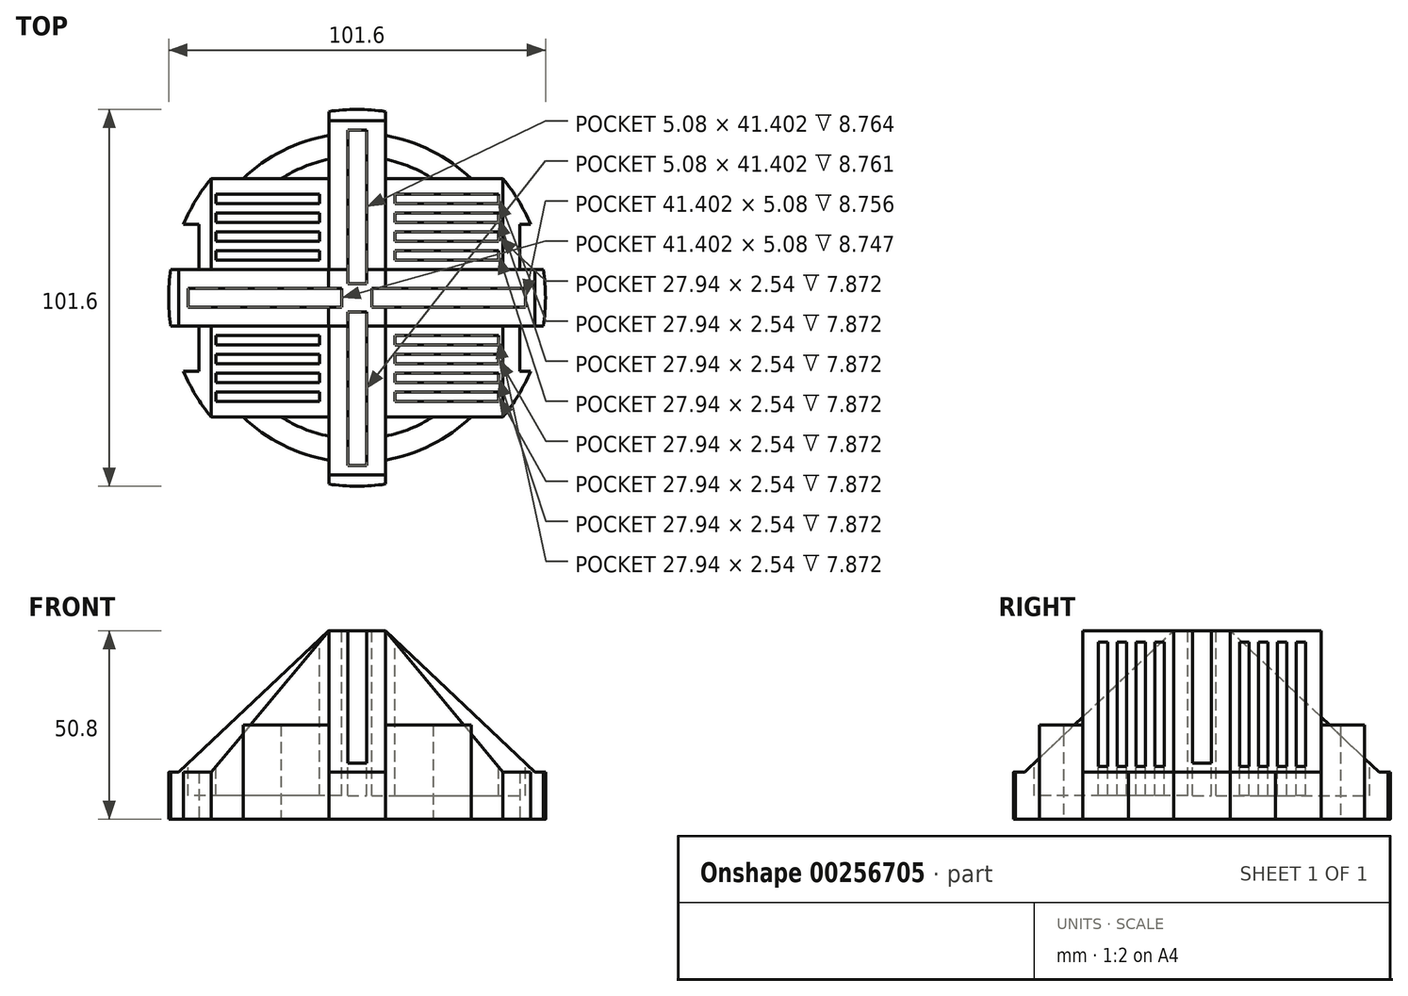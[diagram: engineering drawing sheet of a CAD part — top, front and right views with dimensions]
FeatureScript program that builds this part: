
annotation { "Feature Type Name" : "Feature", "Feature Type Description" : "" }
export const myFeature = defineFeature(function(context is Context, id is Id, definition is map)
    precondition{}
    {
        {
            var Q0;
            Q0=qCreatedBy(makeId("Top.planeOp"),FACE);
            cPlane(context, id + "F0", {"entities" : qUnion([Q0]), "cplaneType" : CPlaneType.OFFSET, "offset" : 50.8 * mm, "width" : 152.4 * mm, "height" : 152.4 * mm});
        }
        {
            var Q0;
            Q0=qCreatedBy(makeId("Top.planeOp"),FACE);
            var sketch = newSketch(context, id + "F1", { "sketchPlane" : qUnion([Q0])});
            skCircle(sketch, "E0", {"center": v(0, 0) * mm, "radius": 50.8 * mm});
            skArc(sketch, "E1", {"start": v(7.62, -43.8) * mm, "mid": v(26.54, -35.66) * mm, "end": v(39.77, -19.86) * mm});
            skArc(sketch, "E2", {"start": v(7.62, -37.33) * mm, "mid": v(38.1, 0) * mm, "end": v(7.62, 37.33) * mm});
            skCircle(sketch, "E3", {"center": v(0, 0) * mm, "radius": 25.4 * mm});
            skLineSegment(sketch, "E4", {"start": v(-7.62, -24.23) * mm, "end": v(-7.62, -50.23) * mm});
            skLineSegment(sketch, "E5", {"start": v(7.62, -24.23) * mm, "end": v(7.62, -50.23) * mm});
            skLineSegment(sketch, "E6", {"start": v(-7.62, 24.23) * mm, "end": v(-7.62, 50.23) * mm});
            skLineSegment(sketch, "E7", {"start": v(7.62, 24.23) * mm, "end": v(7.62, 50.23) * mm});
            skPoint(sketch, "E8.orphan", {"position": v(0, -25.4) * mm});
            skPoint(sketch, "E9.end.orphan", {"position": v(-3.8, -50.66) * mm});
            skArc(sketch, "E10.trimOffspring", {"start": v(-7.62, 37.33) * mm, "mid": v(-38.1, 0) * mm, "end": v(-7.62, -37.33) * mm});
            skArc(sketch, "E11.trimOffspring", {"start": v(-7.62, 43.8) * mm, "mid": v(-26.54, 35.66) * mm, "end": v(-39.77, 19.86) * mm});
            skArc(sketch, "E12", {"start": v(-7.62, -43.8) * mm, "mid": v(0, -44.45) * mm, "end": v(7.62, -43.8) * mm});
            skArc(sketch, "E13", {"start": v(-7.62, -37.33) * mm, "mid": v(0, -38.1) * mm, "end": v(7.62, -37.33) * mm});
            skCircle(sketch, "E14", {"center": v(0, 0) * mm, "radius": 31.75 * mm});
            skArc(sketch, "E15.trimOffspring", {"start": v(7.62, 43.8) * mm, "mid": v(0, 44.45) * mm, "end": v(-7.62, 43.8) * mm});
            skArc(sketch, "E16.trimOffspring", {"start": v(7.62, 37.33) * mm, "mid": v(0, 38.1) * mm, "end": v(-7.62, 37.33) * mm});
            skLineSegment(sketch, "E17", {"start": v(-7.62, -24.23) * mm, "end": v(-7.62, 24.23) * mm});
            skLineSegment(sketch, "E18", {"start": v(7.62, 24.23) * mm, "end": v(7.62, -24.23) * mm});
            skLineSegment(sketch, "E19", {"start": v(0, 7.62) * mm, "end": v(-50.23, 7.62) * mm});
            skLineSegment(sketch, "E20", {"start": v(0, 7.62) * mm, "end": v(50.23, 7.62) * mm});
            skLineSegment(sketch, "E21", {"start": v(0, -7.62) * mm, "end": v(50.23, -7.62) * mm});
            skLineSegment(sketch, "E22", {"start": v(0, -7.62) * mm, "end": v(-50.23, -7.62) * mm});
            skLineSegment(sketch, "E23", {"start": v(-17.78, 7.62) * mm, "end": v(7.62, -17.78) * mm});
            skLineSegment(sketch, "E24", {"start": v(-7.62, 17.78) * mm, "end": v(17.78, -7.62) * mm});
            skLineSegment(sketch, "E25", {"start": v(7.62, 17.78) * mm, "end": v(-17.78, -7.62) * mm});
            skLineSegment(sketch, "E26", {"start": v(17.78, 7.62) * mm, "end": v(-7.62, -17.78) * mm});
            skLineSegment(sketch, "E27", {"start": v(-7.62, -19.86) * mm, "end": v(-20.32, -19.86) * mm});
            skLineSegment(sketch, "E28", {"start": v(-20.32, -19.86) * mm, "end": v(-46.76, -19.86) * mm});
            skLineSegment(sketch, "E29.trimOffspring", {"start": v(-20.32, -32.1) * mm, "end": v(-20.32, -32.23) * mm});
            skPoint(sketch, "E30.start.orphan", {"position": v(-20.32, -7.62) * mm});
            skLineSegment(sketch, "E31", {"start": v(-7.62, -32.1) * mm, "end": v(-39.37, -32.1) * mm});
            skLineSegment(sketch, "E32", {"start": v(-7.62, 19.86) * mm, "end": v(-46.76, 19.86) * mm});
            skLineSegment(sketch, "E33", {"start": v(-7.62, 32.1) * mm, "end": v(-39.37, 32.1) * mm});
            skLineSegment(sketch, "E34", {"start": v(7.62, 32.1) * mm, "end": v(39.37, 32.1) * mm});
            skLineSegment(sketch, "E35", {"start": v(7.62, 19.86) * mm, "end": v(46.76, 19.86) * mm});
            skLineSegment(sketch, "E36", {"start": v(7.62, -19.86) * mm, "end": v(46.76, -19.86) * mm});
            skLineSegment(sketch, "E37", {"start": v(7.62, -32.1) * mm, "end": v(39.37, -32.1) * mm});
            skLineSegment(sketch, "E38", {"start": v(-42.64, 19.86) * mm, "end": v(-42.64, -19.86) * mm});
            skArc(sketch, "E39.trimOffspring", {"start": v(-39.77, -19.86) * mm, "mid": v(-26.54, -35.66) * mm, "end": v(-7.62, -43.8) * mm});
            skLineSegment(sketch, "E40", {"start": v(43.89, -19.86) * mm, "end": v(43.89, 19.86) * mm});
            skArc(sketch, "E41.trimOffspring", {"start": v(39.77, 19.86) * mm, "mid": v(26.54, 35.66) * mm, "end": v(7.62, 43.8) * mm});
            skSolve(sketch);
        }
        {
            var Q0;
            {var subQ5=sQuery(id+"F1.wireOp",EDGE,"E15.trimOffspring");Q0=makeQuery(id+"F1.imprint","IMPRINT",FACE,{"disambiguationData":[TD([[makeQuery(id+"F1.imprint","IMPRINT",EDGE,{"derivedFrom":subQ5}),-1.0]])]});}
            var Q1;
            {var subQ5=sQuery(id+"F1.wireOp",EDGE,"E12");Q1=makeQuery(id+"F1.imprint","IMPRINT",FACE,{"disambiguationData":[TD([[makeQuery(id+"F1.imprint","IMPRINT",EDGE,{"derivedFrom":subQ5}),-1.0]])]});}
            var Q2;
            {var subQ0=sQuery(id+"F1.wireOp",EDGE,"E32");var subQ6=sQuery(id+"F1.wireOp",EDGE,"E0");var subQ7=makeQuery(id+"F1.imprint","INTERSECT",VERTEX,{"derivedFrom":[subQ6,subQ0]});Q2=makeQuery(id+"F1.imprint","IMPRINT",FACE,{"disambiguationData":[TD([[makeQuery(id+"F1.imprint","IMPRINT",EDGE,{"disambiguationData":[TD([[subQ7,1.0]])],"derivedFrom":subQ6}),1.0]])]});}
            var Q3;
            {var subQ0=sQuery(id+"F1.wireOp",EDGE,"E19");var subQ1=sQuery(id+"F1.wireOp",EDGE,"E0");var subQ2=makeQuery(id+"F1.imprint","INTERSECT",VERTEX,{"derivedFrom":[subQ1,subQ0]});Q3=makeQuery(id+"F1.imprint","IMPRINT",FACE,{"disambiguationData":[TD([[makeQuery(id+"F1.imprint","IMPRINT",EDGE,{"disambiguationData":[TD([[subQ2,1.0]])],"derivedFrom":subQ1}),1.0]])]});}
            var Q4;
            {var subQ0=sQuery(id+"F1.wireOp",EDGE,"E19");var subQ1=sQuery(id+"F1.wireOp",EDGE,"E0");var subQ2=makeQuery(id+"F1.imprint","INTERSECT",VERTEX,{"derivedFrom":[subQ1,subQ0]});Q4=makeQuery(id+"F1.imprint","IMPRINT",FACE,{"disambiguationData":[TD([[makeQuery(id+"F1.imprint","IMPRINT",EDGE,{"disambiguationData":[TD([[subQ2,-1.0]])],"derivedFrom":subQ1}),1.0]])]});}
            var Q5;
            {var subQ0=sQuery(id+"F1.wireOp",EDGE,"E22");var subQ1=sQuery(id+"F1.wireOp",EDGE,"E0");var subQ2=makeQuery(id+"F1.imprint","INTERSECT",VERTEX,{"derivedFrom":[subQ1,subQ0]});Q5=makeQuery(id+"F1.imprint","IMPRINT",FACE,{"disambiguationData":[TD([[makeQuery(id+"F1.imprint","IMPRINT",EDGE,{"disambiguationData":[TD([[subQ2,-1.0]])],"derivedFrom":subQ1}),1.0]])]});}
            var Q6;
            {var subQ0=sQuery(id+"F1.wireOp",EDGE,"E28");var subQ4=sQuery(id+"F1.wireOp",EDGE,"E0");var subQ5=makeQuery(id+"F1.imprint","INTERSECT",VERTEX,{"derivedFrom":[subQ4,subQ0]});Q6=makeQuery(id+"F1.imprint","IMPRINT",FACE,{"disambiguationData":[TD([[makeQuery(id+"F1.imprint","IMPRINT",EDGE,{"disambiguationData":[TD([[subQ5,-1.0]])],"derivedFrom":subQ4}),1.0]])]});}
            var Q7;
            {var subQ1=sQuery(id+"F1.wireOp",EDGE,"E0");var subQ6=sQuery(id+"F1.wireOp",EDGE,"E34");var subQ8=makeQuery(id+"F1.imprint","INTERSECT",VERTEX,{"derivedFrom":[subQ1,subQ6]});Q7=makeQuery(id+"F1.imprint","IMPRINT",FACE,{"disambiguationData":[TD([[makeQuery(id+"F1.imprint","IMPRINT",EDGE,{"disambiguationData":[TD([[subQ8,1.0]])],"derivedFrom":subQ1}),1.0]])]});}
            var Q8;
            {var subQ0=sQuery(id+"F1.wireOp",EDGE,"E20");var subQ1=sQuery(id+"F1.wireOp",EDGE,"E0");var subQ2=makeQuery(id+"F1.imprint","INTERSECT",VERTEX,{"derivedFrom":[subQ1,subQ0]});Q8=makeQuery(id+"F1.imprint","IMPRINT",FACE,{"disambiguationData":[TD([[makeQuery(id+"F1.imprint","IMPRINT",EDGE,{"disambiguationData":[TD([[subQ2,-1.0]])],"derivedFrom":subQ1}),1.0]])]});}
            var Q9;
            {var subQ1=sQuery(id+"F1.wireOp",EDGE,"E0");var subQ5=sQuery(id+"F1.wireOp",EDGE,"E20");var subQ6=makeQuery(id+"F1.imprint","INTERSECT",VERTEX,{"derivedFrom":[subQ1,subQ5]});Q9=makeQuery(id+"F1.imprint","IMPRINT",FACE,{"disambiguationData":[TD([[makeQuery(id+"F1.imprint","IMPRINT",EDGE,{"disambiguationData":[TD([[subQ6,1.0]])],"derivedFrom":subQ1}),1.0]])]});}
            var Q10;
            {var subQ0=sQuery(id+"F1.wireOp",EDGE,"E21");var subQ1=sQuery(id+"F1.wireOp",EDGE,"E0");var subQ2=makeQuery(id+"F1.imprint","INTERSECT",VERTEX,{"derivedFrom":[subQ1,subQ0]});Q10=makeQuery(id+"F1.imprint","IMPRINT",FACE,{"disambiguationData":[TD([[makeQuery(id+"F1.imprint","IMPRINT",EDGE,{"disambiguationData":[TD([[subQ2,1.0]])],"derivedFrom":subQ1}),1.0]])]});}
            var Q11;
            {var subQ0=sQuery(id+"F1.wireOp",EDGE,"E36");var subQ1=sQuery(id+"F1.wireOp",EDGE,"E0");var subQ2=makeQuery(id+"F1.imprint","INTERSECT",VERTEX,{"derivedFrom":[subQ1,subQ0]});Q11=makeQuery(id+"F1.imprint","IMPRINT",FACE,{"disambiguationData":[TD([[makeQuery(id+"F1.imprint","IMPRINT",EDGE,{"disambiguationData":[TD([[subQ2,1.0]])],"derivedFrom":subQ1}),1.0]])]});}
            var Q12;
            {var subQ0=sQuery(id+"F1.wireOp",EDGE,"E4");var subQ1=sQuery(id+"F1.wireOp",EDGE,"E0");var subQ2=makeQuery(id+"F1.imprint","INTERSECT",VERTEX,{"derivedFrom":[subQ1,subQ0]});Q12=makeQuery(id+"F1.imprint","IMPRINT",FACE,{"disambiguationData":[TD([[makeQuery(id+"F1.imprint","IMPRINT",EDGE,{"disambiguationData":[TD([[subQ2,1.0]])],"derivedFrom":subQ1}),1.0]])]});}
            var Q13;
            {var subQ0=sQuery(id+"F1.wireOp",EDGE,"E6");var subQ1=sQuery(id+"F1.wireOp",EDGE,"E0");var subQ2=makeQuery(id+"F1.imprint","INTERSECT",VERTEX,{"derivedFrom":[subQ1,subQ0]});Q13=makeQuery(id+"F1.imprint","IMPRINT",FACE,{"disambiguationData":[TD([[makeQuery(id+"F1.imprint","IMPRINT",EDGE,{"disambiguationData":[TD([[subQ2,-1.0]])],"derivedFrom":subQ1}),1.0]])]});}
            var Q14;
            {var subQ0=sQuery(id+"F1.wireOp",EDGE,"E7");var subQ1=sQuery(id+"F1.wireOp",EDGE,"E0");var subQ2=makeQuery(id+"F1.imprint","INTERSECT",VERTEX,{"derivedFrom":[subQ1,subQ0]});Q14=makeQuery(id+"F1.imprint","IMPRINT",FACE,{"disambiguationData":[TD([[makeQuery(id+"F1.imprint","IMPRINT",EDGE,{"disambiguationData":[TD([[subQ2,1.0]])],"derivedFrom":subQ1}),1.0]])]});}
            var Q15;
            {var subQ0=sQuery(id+"F1.wireOp",EDGE,"E5");var subQ1=sQuery(id+"F1.wireOp",EDGE,"E0");var subQ2=makeQuery(id+"F1.imprint","INTERSECT",VERTEX,{"derivedFrom":[subQ1,subQ0]});Q15=makeQuery(id+"F1.imprint","IMPRINT",FACE,{"disambiguationData":[TD([[makeQuery(id+"F1.imprint","IMPRINT",EDGE,{"disambiguationData":[TD([[subQ2,-1.0]])],"derivedFrom":subQ1}),1.0]])]});}
            extrude(context, id + "F2", {"entities" : qUnion([Q0, Q1, Q2, Q3, Q4, Q5, Q6, Q7, Q8, Q9, Q10, Q11, Q12, Q13, Q14, Q15]), "depth" : 12.7 * mm});
        }
        {
            var Q0;
            {var subQ0=sQuery(id+"F1.wireOp",EDGE,"E10.trimOffspring");Q0=makeQuery(id+"F1.imprint","IMPRINT",FACE,{"disambiguationData":[TD([[makeQuery(id+"F1.imprint","IMPRINT",EDGE,{"derivedFrom":subQ0}),-1.0]])]});}
            var Q1;
            {var subQ0=sQuery(id+"F1.wireOp",EDGE,"E1");Q1=makeQuery(id+"F1.imprint","IMPRINT",FACE,{"disambiguationData":[TD([[makeQuery(id+"F1.imprint","IMPRINT",EDGE,{"derivedFrom":subQ0}),1.0]])]});}
            var Q2;
            {var subQ2=sQuery(id+"F1.wireOp",EDGE,"E15.trimOffspring");Q2=makeQuery(id+"F1.imprint","IMPRINT",FACE,{"disambiguationData":[TD([[makeQuery(id+"F1.imprint","IMPRINT",EDGE,{"derivedFrom":subQ2}),1.0]])]});}
            var Q3;
            {var subQ2=sQuery(id+"F1.wireOp",EDGE,"E12");Q3=makeQuery(id+"F1.imprint","IMPRINT",FACE,{"disambiguationData":[TD([[makeQuery(id+"F1.imprint","IMPRINT",EDGE,{"derivedFrom":subQ2}),1.0]])]});}
            var Q4;
            {var subQ0=sQuery(id+"F1.wireOp",EDGE,"E10.trimOffspring");var subQ5=sQuery(id+"F1.wireOp",EDGE,"KU0cdiGB-8eOj-Trs3-v5YD-3LzdnCRRimhK");var subQ6=makeQuery(id+"F1.imprint","INTERSECT",VERTEX,{"derivedFrom":[subQ0,subQ5]});Q4=makeQuery(id+"F1.imprint","IMPRINT",FACE,{"disambiguationData":[TD([[makeQuery(id+"F1.imprint","IMPRINT",EDGE,{"disambiguationData":[TD([[subQ6,-1.0]])],"derivedFrom":subQ5}),-1.0]])]});}
            var Q5;
            {var subQ0=sQuery(id+"F1.wireOp",EDGE,"KU0cdiGB-8eOj-Trs3-v5YD-3LzdnCRRimhK");var subQ1=sQuery(id+"F1.wireOp",EDGE,"E10.trimOffspring");var subQ2=makeQuery(id+"F1.imprint","INTERSECT",VERTEX,{"derivedFrom":[subQ1,subQ0]});Q5=makeQuery(id+"F1.imprint","IMPRINT",FACE,{"disambiguationData":[TD([[makeQuery(id+"F1.imprint","IMPRINT",EDGE,{"disambiguationData":[TD([[subQ2,-1.0]])],"derivedFrom":subQ1}),-1.0]])]});}
            var Q6;
            {var subQ0=sQuery(id+"F1.wireOp",EDGE,"n5LII22h-w08l-qE72-yfr9-18N67uZxNTdQ");var subQ1=sQuery(id+"F1.wireOp",EDGE,"E10.trimOffspring");var subQ2=makeQuery(id+"F1.imprint","INTERSECT",VERTEX,{"derivedFrom":[subQ1,subQ0]});Q6=makeQuery(id+"F1.imprint","IMPRINT",FACE,{"disambiguationData":[TD([[makeQuery(id+"F1.imprint","IMPRINT",EDGE,{"disambiguationData":[TD([[subQ2,-1.0]])],"derivedFrom":subQ1}),-1.0]])]});}
            var Q7;
            {var subQ0=sQuery(id+"F1.wireOp",EDGE,"E19");var subQ1=sQuery(id+"F1.wireOp",EDGE,"E10.trimOffspring");var subQ2=makeQuery(id+"F1.imprint","INTERSECT",VERTEX,{"derivedFrom":[subQ1,subQ0]});Q7=makeQuery(id+"F1.imprint","IMPRINT",FACE,{"disambiguationData":[TD([[makeQuery(id+"F1.imprint","IMPRINT",EDGE,{"disambiguationData":[TD([[subQ2,-1.0]])],"derivedFrom":subQ1}),-1.0]])]});}
            var Q8;
            {var subQ0=sQuery(id+"F1.wireOp",EDGE,"E22");var subQ1=sQuery(id+"F1.wireOp",EDGE,"E10.trimOffspring");var subQ2=makeQuery(id+"F1.imprint","INTERSECT",VERTEX,{"derivedFrom":[subQ1,subQ0]});Q8=makeQuery(id+"F1.imprint","IMPRINT",FACE,{"disambiguationData":[TD([[makeQuery(id+"F1.imprint","IMPRINT",EDGE,{"disambiguationData":[TD([[subQ2,-1.0]])],"derivedFrom":subQ1}),-1.0]])]});}
            var Q9;
            {var subQ0=sQuery(id+"F1.wireOp",EDGE,"E28");var subQ1=sQuery(id+"F1.wireOp",EDGE,"E10.trimOffspring");var subQ2=makeQuery(id+"F1.imprint","INTERSECT",VERTEX,{"derivedFrom":[subQ1,subQ0]});Q9=makeQuery(id+"F1.imprint","IMPRINT",FACE,{"disambiguationData":[TD([[makeQuery(id+"F1.imprint","IMPRINT",EDGE,{"disambiguationData":[TD([[subQ2,-1.0]])],"derivedFrom":subQ1}),-1.0]])]});}
            var Q10;
            {var subQ1=sQuery(id+"F1.wireOp",EDGE,"E10.trimOffspring");var subQ5=sQuery(id+"F1.wireOp",EDGE,"E25");var subQ6=makeQuery(id+"F1.imprint","INTERSECT",VERTEX,{"derivedFrom":[subQ1,subQ5]});Q10=makeQuery(id+"F1.imprint","IMPRINT",FACE,{"disambiguationData":[TD([[makeQuery(id+"F1.imprint","IMPRINT",EDGE,{"disambiguationData":[TD([[subQ6,-1.0]])],"derivedFrom":subQ1}),-1.0]])]});}
            var Q11;
            {var subQ0=sQuery(id+"F1.wireOp",EDGE,"E31");var subQ1=sQuery(id+"F1.wireOp",EDGE,"E11.trimOffspring");var subQ2=makeQuery(id+"F1.imprint","INTERSECT",VERTEX,{"derivedFrom":[subQ1,subQ0]});Q11=makeQuery(id+"F1.imprint","IMPRINT",FACE,{"disambiguationData":[TD([[makeQuery(id+"F1.imprint","IMPRINT",EDGE,{"disambiguationData":[TD([[subQ2,-1.0]])],"derivedFrom":subQ1}),1.0]])]});}
            var Q12;
            {var subQ0=sQuery(id+"F1.wireOp",EDGE,"E26");var subQ1=sQuery(id+"F1.wireOp",EDGE,"E10.trimOffspring");var subQ2=makeQuery(id+"F1.imprint","INTERSECT",VERTEX,{"derivedFrom":[subQ1,subQ0]});Q12=makeQuery(id+"F1.imprint","IMPRINT",FACE,{"disambiguationData":[TD([[makeQuery(id+"F1.imprint","IMPRINT",EDGE,{"disambiguationData":[TD([[subQ2,-1.0]])],"derivedFrom":subQ1}),-1.0]])]});}
            var Q13;
            {var subQ0=sQuery(id+"F1.wireOp",EDGE,"E32");var subQ1=sQuery(id+"F1.wireOp",EDGE,"E10.trimOffspring");var subQ2=makeQuery(id+"F1.imprint","INTERSECT",VERTEX,{"derivedFrom":[subQ1,subQ0]});Q13=makeQuery(id+"F1.imprint","IMPRINT",FACE,{"disambiguationData":[TD([[makeQuery(id+"F1.imprint","IMPRINT",EDGE,{"disambiguationData":[TD([[subQ2,-1.0]])],"derivedFrom":subQ1}),-1.0]])]});}
            var Q14;
            {var subQ0=sQuery(id+"F1.wireOp",EDGE,"E33");var subQ1=sQuery(id+"F1.wireOp",EDGE,"E10.trimOffspring");var subQ2=makeQuery(id+"F1.imprint","INTERSECT",VERTEX,{"derivedFrom":[subQ1,subQ0]});Q14=makeQuery(id+"F1.imprint","IMPRINT",FACE,{"disambiguationData":[TD([[makeQuery(id+"F1.imprint","IMPRINT",EDGE,{"disambiguationData":[TD([[subQ2,-1.0]])],"derivedFrom":subQ1}),-1.0]])]});}
            var Q15;
            {var subQ0=sQuery(id+"F1.wireOp",EDGE,"E10.trimOffspring");var subQ5=sQuery(id+"F1.wireOp",EDGE,"E33");var subQ7=makeQuery(id+"F1.imprint","INTERSECT",VERTEX,{"derivedFrom":[subQ0,subQ5]});Q15=makeQuery(id+"F1.imprint","IMPRINT",FACE,{"disambiguationData":[TD([[makeQuery(id+"F1.imprint","IMPRINT",EDGE,{"disambiguationData":[TD([[subQ7,-1.0]])],"derivedFrom":subQ5}),-1.0]])]});}
            var Q16;
            {var subQ0=sQuery(id+"F1.wireOp",EDGE,"E35");var subQ1=sQuery(id+"F1.wireOp",EDGE,"E2");var subQ2=makeQuery(id+"F1.imprint","INTERSECT",VERTEX,{"derivedFrom":[subQ1,subQ0]});Q16=makeQuery(id+"F1.imprint","IMPRINT",FACE,{"disambiguationData":[TD([[makeQuery(id+"F1.imprint","IMPRINT",EDGE,{"disambiguationData":[TD([[subQ2,-1.0]])],"derivedFrom":subQ1}),-1.0]])]});}
            var Q17;
            {var subQ0=sQuery(id+"F1.wireOp",EDGE,"E20");var subQ6=sQuery(id+"F1.wireOp",EDGE,"E2");var subQ8=makeQuery(id+"F1.imprint","INTERSECT",VERTEX,{"derivedFrom":[subQ6,subQ0]});Q17=makeQuery(id+"F1.imprint","IMPRINT",FACE,{"disambiguationData":[TD([[makeQuery(id+"F1.imprint","IMPRINT",EDGE,{"disambiguationData":[TD([[subQ8,-1.0]])],"derivedFrom":subQ6}),-1.0]])]});}
            var Q18;
            {var subQ0=sQuery(id+"F1.wireOp",EDGE,"18cd6810-feed-407b-96fd-876ede30ebc9.trimOffspring");Q18=makeQuery(id+"F1.imprint","IMPRINT",FACE,{"disambiguationData":[TD([[makeQuery(id+"F1.imprint","IMPRINT",EDGE,{"derivedFrom":subQ0}),1.0]])]});}
            var Q19;
            {var subQ0=sQuery(id+"F1.wireOp",EDGE,"E36");var subQ2=sQuery(id+"F1.wireOp",EDGE,"E2");var subQ3=makeQuery(id+"F1.imprint","INTERSECT",VERTEX,{"derivedFrom":[subQ2,subQ0]});Q19=makeQuery(id+"F1.imprint","IMPRINT",FACE,{"disambiguationData":[TD([[makeQuery(id+"F1.imprint","IMPRINT",EDGE,{"disambiguationData":[TD([[subQ3,-1.0]])],"derivedFrom":subQ2}),-1.0]])]});}
            var Q20;
            {var subQ0=sQuery(id+"F1.wireOp",EDGE,"E21");var subQ1=sQuery(id+"F1.wireOp",EDGE,"E2");var subQ2=makeQuery(id+"F1.imprint","INTERSECT",VERTEX,{"derivedFrom":[subQ1,subQ0]});Q20=makeQuery(id+"F1.imprint","IMPRINT",FACE,{"disambiguationData":[TD([[makeQuery(id+"F1.imprint","IMPRINT",EDGE,{"disambiguationData":[TD([[subQ2,-1.0]])],"derivedFrom":subQ1}),-1.0]])]});}
            var Q21;
            {var subQ1=sQuery(id+"F1.wireOp",EDGE,"E2");var subQ3=sQuery(id+"F1.wireOp",EDGE,"E34");var subQ4=makeQuery(id+"F1.imprint","INTERSECT",VERTEX,{"derivedFrom":[subQ1,subQ3]});Q21=makeQuery(id+"F1.imprint","IMPRINT",FACE,{"disambiguationData":[TD([[makeQuery(id+"F1.imprint","IMPRINT",EDGE,{"disambiguationData":[TD([[subQ4,-1.0]])],"derivedFrom":subQ3}),1.0]])]});}
            extrude(context, id + "F3", {"entities" : qUnion([Q0, Q1, Q2, Q3, Q4, Q5, Q6, Q7, Q8, Q9, Q10, Q11, Q12, Q13, Q14, Q15, Q16, Q17, Q18, Q19, Q20, Q21]), "operationType" : NewBodyOperationType.ADD, "depth" : 25.4 * mm});
        }
        {
            var Q0;
            {var subQ0=sQuery(id+"F1.wireOp",EDGE,"E13");Q0=makeQuery(id+"F1.imprint","IMPRINT",FACE,{"disambiguationData":[TD([[makeQuery(id+"F1.imprint","IMPRINT",EDGE,{"derivedFrom":subQ0}),1.0]])]});}
            var Q1;
            {var subQ0=sQuery(id+"F1.wireOp",EDGE,"E10.trimOffspring");Q1=makeQuery(id+"F1.imprint","IMPRINT",FACE,{"disambiguationData":[TD([[makeQuery(id+"F1.imprint","IMPRINT",EDGE,{"derivedFrom":subQ0}),1.0]])]});}
            var Q2;
            {var subQ0=sQuery(id+"F1.wireOp",EDGE,"E2");Q2=makeQuery(id+"F1.imprint","IMPRINT",FACE,{"disambiguationData":[TD([[makeQuery(id+"F1.imprint","IMPRINT",EDGE,{"derivedFrom":subQ0}),1.0]])]});}
            var Q3;
            {var subQ0=sQuery(id+"F1.wireOp",EDGE,"E16.trimOffspring");Q3=makeQuery(id+"F1.imprint","IMPRINT",FACE,{"disambiguationData":[TD([[makeQuery(id+"F1.imprint","IMPRINT",EDGE,{"derivedFrom":subQ0}),1.0]])]});}
            var Q4;
            {var subQ0=sQuery(id+"F1.wireOp",EDGE,"n5LII22h-w08l-qE72-yfr9-18N67uZxNTdQ");var subQ1=sQuery(id+"F1.wireOp",EDGE,"E10.trimOffspring");var subQ2=makeQuery(id+"F1.imprint","INTERSECT",VERTEX,{"derivedFrom":[subQ1,subQ0]});Q4=makeQuery(id+"F1.imprint","IMPRINT",FACE,{"disambiguationData":[TD([[makeQuery(id+"F1.imprint","IMPRINT",EDGE,{"disambiguationData":[TD([[subQ2,-1.0]])],"derivedFrom":subQ1}),1.0]])]});}
            var Q5;
            {var subQ0=sQuery(id+"F1.wireOp",EDGE,"KU0cdiGB-8eOj-Trs3-v5YD-3LzdnCRRimhK");var subQ1=sQuery(id+"F1.wireOp",EDGE,"E10.trimOffspring");var subQ2=makeQuery(id+"F1.imprint","INTERSECT",VERTEX,{"derivedFrom":[subQ1,subQ0]});Q5=makeQuery(id+"F1.imprint","IMPRINT",FACE,{"disambiguationData":[TD([[makeQuery(id+"F1.imprint","IMPRINT",EDGE,{"disambiguationData":[TD([[subQ2,-1.0]])],"derivedFrom":subQ1}),1.0]])]});}
            var Q6;
            {var subQ1=sQuery(id+"F1.wireOp",EDGE,"E6");var subQ3=sQuery(id+"F1.wireOp",EDGE,"E14");var subQ4=makeQuery(id+"F1.imprint","INTERSECT",VERTEX,{"derivedFrom":[subQ1,subQ3]});Q6=makeQuery(id+"F1.imprint","IMPRINT",FACE,{"disambiguationData":[TD([[makeQuery(id+"F1.imprint","IMPRINT",EDGE,{"disambiguationData":[TD([[subQ4,-1.0]])],"derivedFrom":subQ3}),-1.0]])]});}
            var Q7;
            {var subQ0=sQuery(id+"F1.wireOp",EDGE,"E7");var subQ5=sQuery(id+"F1.wireOp",EDGE,"E14");var subQ6=makeQuery(id+"F1.imprint","INTERSECT",VERTEX,{"derivedFrom":[subQ0,subQ5]});Q7=makeQuery(id+"F1.imprint","IMPRINT",FACE,{"disambiguationData":[TD([[makeQuery(id+"F1.imprint","IMPRINT",EDGE,{"disambiguationData":[TD([[subQ6,1.0]])],"derivedFrom":subQ5}),-1.0]])]});}
            var Q8;
            {var subQ0=sQuery(id+"F1.wireOp",EDGE,"E19");var subQ1=sQuery(id+"F1.wireOp",EDGE,"E10.trimOffspring");var subQ2=makeQuery(id+"F1.imprint","INTERSECT",VERTEX,{"derivedFrom":[subQ1,subQ0]});Q8=makeQuery(id+"F1.imprint","IMPRINT",FACE,{"disambiguationData":[TD([[makeQuery(id+"F1.imprint","IMPRINT",EDGE,{"disambiguationData":[TD([[subQ2,-1.0]])],"derivedFrom":subQ1}),1.0]])]});}
            var Q9;
            {var subQ0=sQuery(id+"F1.wireOp",EDGE,"E22");var subQ1=sQuery(id+"F1.wireOp",EDGE,"E10.trimOffspring");var subQ2=makeQuery(id+"F1.imprint","INTERSECT",VERTEX,{"derivedFrom":[subQ1,subQ0]});Q9=makeQuery(id+"F1.imprint","IMPRINT",FACE,{"disambiguationData":[TD([[makeQuery(id+"F1.imprint","IMPRINT",EDGE,{"disambiguationData":[TD([[subQ2,-1.0]])],"derivedFrom":subQ1}),1.0]])]});}
            var Q10;
            {var subQ0=sQuery(id+"F1.wireOp",EDGE,"E25");var subQ1=sQuery(id+"F1.wireOp",EDGE,"E10.trimOffspring");var subQ2=makeQuery(id+"F1.imprint","INTERSECT",VERTEX,{"derivedFrom":[subQ1,subQ0]});Q10=makeQuery(id+"F1.imprint","IMPRINT",FACE,{"disambiguationData":[TD([[makeQuery(id+"F1.imprint","IMPRINT",EDGE,{"disambiguationData":[TD([[subQ2,-1.0]])],"derivedFrom":subQ1}),1.0]])]});}
            var Q11;
            {var subQ3=sQuery(id+"F1.wireOp",EDGE,"E14");var subQ7=sQuery(id+"F1.wireOp",EDGE,"E4");var subQ8=makeQuery(id+"F1.imprint","INTERSECT",VERTEX,{"derivedFrom":[subQ7,subQ3]});Q11=makeQuery(id+"F1.imprint","IMPRINT",FACE,{"disambiguationData":[TD([[makeQuery(id+"F1.imprint","IMPRINT",EDGE,{"disambiguationData":[TD([[subQ8,-1.0]])],"derivedFrom":subQ7}),-1.0]])]});}
            var Q12;
            {var subQ1=sQuery(id+"F1.wireOp",EDGE,"E2");var subQ5=sQuery(id+"F1.wireOp",EDGE,"dChad7VG-r3lr-Y0ra-zuCQ-UW0r8UzcO7aT");var subQ6=makeQuery(id+"F1.imprint","INTERSECT",VERTEX,{"derivedFrom":[subQ1,subQ5]});Q12=makeQuery(id+"F1.imprint","IMPRINT",FACE,{"disambiguationData":[TD([[makeQuery(id+"F1.imprint","IMPRINT",EDGE,{"disambiguationData":[TD([[subQ6,-1.0]])],"derivedFrom":subQ1}),1.0]])]});}
            var Q13;
            {var subQ0=sQuery(id+"F1.wireOp",EDGE,"E23");var subQ1=sQuery(id+"F1.wireOp",EDGE,"E2");var subQ2=makeQuery(id+"F1.imprint","INTERSECT",VERTEX,{"derivedFrom":[subQ1,subQ0]});Q13=makeQuery(id+"F1.imprint","IMPRINT",FACE,{"disambiguationData":[TD([[makeQuery(id+"F1.imprint","IMPRINT",EDGE,{"disambiguationData":[TD([[subQ2,-1.0]])],"derivedFrom":subQ1}),1.0]])]});}
            var Q14;
            {var subQ0=sQuery(id+"F1.wireOp",EDGE,"E24");var subQ1=sQuery(id+"F1.wireOp",EDGE,"E2");var subQ2=makeQuery(id+"F1.imprint","INTERSECT",VERTEX,{"derivedFrom":[subQ1,subQ0]});Q14=makeQuery(id+"F1.imprint","IMPRINT",FACE,{"disambiguationData":[TD([[makeQuery(id+"F1.imprint","IMPRINT",EDGE,{"disambiguationData":[TD([[subQ2,-1.0]])],"derivedFrom":subQ1}),1.0]])]});}
            var Q15;
            {var subQ0=sQuery(id+"F1.wireOp",EDGE,"E21");var subQ1=sQuery(id+"F1.wireOp",EDGE,"E2");var subQ2=makeQuery(id+"F1.imprint","INTERSECT",VERTEX,{"derivedFrom":[subQ1,subQ0]});Q15=makeQuery(id+"F1.imprint","IMPRINT",FACE,{"disambiguationData":[TD([[makeQuery(id+"F1.imprint","IMPRINT",EDGE,{"disambiguationData":[TD([[subQ2,-1.0]])],"derivedFrom":subQ1}),1.0]])]});}
            var Q16;
            {var subQ0=sQuery(id+"F1.wireOp",EDGE,"E20");var subQ1=sQuery(id+"F1.wireOp",EDGE,"E2");var subQ2=makeQuery(id+"F1.imprint","INTERSECT",VERTEX,{"derivedFrom":[subQ1,subQ0]});Q16=makeQuery(id+"F1.imprint","IMPRINT",FACE,{"disambiguationData":[TD([[makeQuery(id+"F1.imprint","IMPRINT",EDGE,{"disambiguationData":[TD([[subQ2,-1.0]])],"derivedFrom":subQ1}),1.0]])]});}
            var Q17;
            {var subQ0=sQuery(id+"F1.wireOp",EDGE,"SVIod6WE-LFFt-Ms97-owyS-8ShU65W6W8it");var subQ1=sQuery(id+"F1.wireOp",EDGE,"E2");var subQ2=makeQuery(id+"F1.imprint","INTERSECT",VERTEX,{"derivedFrom":[subQ1,subQ0]});Q17=makeQuery(id+"F1.imprint","IMPRINT",FACE,{"disambiguationData":[TD([[makeQuery(id+"F1.imprint","IMPRINT",EDGE,{"disambiguationData":[TD([[subQ2,-1.0]])],"derivedFrom":subQ1}),1.0]])]});}
            var Q18;
            {var subQ0=sQuery(id+"F1.wireOp",EDGE,"E25");var subQ1=sQuery(id+"F1.wireOp",EDGE,"E14");var subQ2=makeQuery(id+"F1.imprint","INTERSECT",VERTEX,{"derivedFrom":[subQ1,subQ0]});Q18=makeQuery(id+"F1.imprint","IMPRINT",FACE,{"disambiguationData":[TD([[makeQuery(id+"F1.imprint","IMPRINT",EDGE,{"disambiguationData":[TD([[subQ2,-1.0]])],"derivedFrom":subQ1}),-1.0]])]});}
            var Q19;
            {var subQ0=sQuery(id+"F1.wireOp",EDGE,"E30");var subQ1=sQuery(id+"F1.wireOp",EDGE,"E14");var subQ2=makeQuery(id+"F1.imprint","INTERSECT",VERTEX,{"derivedFrom":[subQ1,subQ0]});Q19=makeQuery(id+"F1.imprint","IMPRINT",FACE,{"disambiguationData":[TD([[makeQuery(id+"F1.imprint","IMPRINT",EDGE,{"disambiguationData":[TD([[subQ2,-1.0]])],"derivedFrom":subQ1}),-1.0]])]});}
            var Q20;
            {var subQ5=sQuery(id+"F1.wireOp",EDGE,"E29.trimOffspring");Q20=makeQuery(id+"F1.imprint","IMPRINT",FACE,{"disambiguationData":[TD([[makeQuery(id+"F1.imprint","IMPRINT",EDGE,{"derivedFrom":subQ5}),1.0]])]});}
            var Q21;
            {var subQ1=sQuery(id+"F1.wireOp",EDGE,"E2");var subQ7=sQuery(id+"F1.wireOp",EDGE,"E37");var subQ9=makeQuery(id+"F1.imprint","INTERSECT",VERTEX,{"derivedFrom":[subQ1,subQ7]});Q21=makeQuery(id+"F1.imprint","IMPRINT",FACE,{"disambiguationData":[TD([[makeQuery(id+"F1.imprint","IMPRINT",EDGE,{"disambiguationData":[TD([[subQ9,-1.0]])],"derivedFrom":subQ1}),1.0]])]});}
            extrude(context, id + "F4", {"entities" : qUnion([Q0, Q1, Q2, Q3, Q4, Q5, Q6, Q7, Q8, Q9, Q10, Q11, Q12, Q13, Q14, Q15, Q16, Q17, Q18, Q19, Q20, Q21]), "operationType" : NewBodyOperationType.ADD, "depth" : 38.1 * mm});
        }
        {
            var Q0;
            {var subQ0=sQuery(id+"F1.wireOp",EDGE,"E6");var subQ1=sQuery(id+"F1.wireOp",EDGE,"E3");var subQ2=makeQuery(id+"F1.imprint","INTERSECT",VERTEX,{"derivedFrom":[subQ1,subQ0]});Q0=makeQuery(id+"F1.imprint","IMPRINT",FACE,{"disambiguationData":[TD([[makeQuery(id+"F1.imprint","IMPRINT",EDGE,{"disambiguationData":[TD([[subQ2,1.0]])],"derivedFrom":subQ1}),-1.0]])]});}
            var Q1;
            {var subQ0=sQuery(id+"F1.wireOp",EDGE,"E4");var subQ1=sQuery(id+"F1.wireOp",EDGE,"E3");var subQ2=makeQuery(id+"F1.imprint","INTERSECT",VERTEX,{"derivedFrom":[subQ1,subQ0]});Q1=makeQuery(id+"F1.imprint","IMPRINT",FACE,{"disambiguationData":[TD([[makeQuery(id+"F1.imprint","IMPRINT",EDGE,{"disambiguationData":[TD([[subQ2,-1.0]])],"derivedFrom":subQ1}),-1.0]])]});}
            var Q2;
            {var subQ0=sQuery(id+"F1.wireOp",EDGE,"E5");var subQ1=sQuery(id+"F1.wireOp",EDGE,"E3");var subQ2=makeQuery(id+"F1.imprint","INTERSECT",VERTEX,{"derivedFrom":[subQ1,subQ0]});Q2=makeQuery(id+"F1.imprint","IMPRINT",FACE,{"disambiguationData":[TD([[makeQuery(id+"F1.imprint","IMPRINT",EDGE,{"disambiguationData":[TD([[subQ2,-1.0]])],"derivedFrom":subQ1}),-1.0]])]});}
            var Q3;
            {var subQ0=sQuery(id+"F1.wireOp",EDGE,"E7");var subQ5=sQuery(id+"F1.wireOp",EDGE,"E14");var subQ6=makeQuery(id+"F1.imprint","INTERSECT",VERTEX,{"derivedFrom":[subQ0,subQ5]});Q3=makeQuery(id+"F1.imprint","IMPRINT",FACE,{"disambiguationData":[TD([[makeQuery(id+"F1.imprint","IMPRINT",EDGE,{"disambiguationData":[TD([[subQ6,1.0]])],"derivedFrom":subQ5}),1.0]])]});}
            var Q4;
            {var subQ0=sQuery(id+"F1.wireOp",EDGE,"E19");var subQ1=sQuery(id+"F1.wireOp",EDGE,"E3");var subQ2=makeQuery(id+"F1.imprint","INTERSECT",VERTEX,{"derivedFrom":[subQ1,subQ0]});Q4=makeQuery(id+"F1.imprint","IMPRINT",FACE,{"disambiguationData":[TD([[makeQuery(id+"F1.imprint","IMPRINT",EDGE,{"disambiguationData":[TD([[subQ2,-1.0]])],"derivedFrom":subQ1}),-1.0]])]});}
            var Q5;
            {var subQ0=sQuery(id+"F1.wireOp",EDGE,"E6");var subQ5=sQuery(id+"F1.wireOp",EDGE,"E14");var subQ6=makeQuery(id+"F1.imprint","INTERSECT",VERTEX,{"derivedFrom":[subQ0,subQ5]});Q5=makeQuery(id+"F1.imprint","IMPRINT",FACE,{"disambiguationData":[TD([[makeQuery(id+"F1.imprint","IMPRINT",EDGE,{"disambiguationData":[TD([[subQ6,-1.0]])],"derivedFrom":subQ5}),1.0]])]});}
            var Q6;
            {var subQ0=sQuery(id+"F1.wireOp",EDGE,"E20");var subQ1=sQuery(id+"F1.wireOp",EDGE,"E3");var subQ2=makeQuery(id+"F1.imprint","INTERSECT",VERTEX,{"derivedFrom":[subQ1,subQ0]});Q6=makeQuery(id+"F1.imprint","IMPRINT",FACE,{"disambiguationData":[TD([[makeQuery(id+"F1.imprint","IMPRINT",EDGE,{"disambiguationData":[TD([[subQ2,1.0]])],"derivedFrom":subQ1}),-1.0]])]});}
            var Q7;
            {var subQ1=sQuery(id+"F1.wireOp",EDGE,"E4");var subQ3=sQuery(id+"F1.wireOp",EDGE,"E14");var subQ4=makeQuery(id+"F1.imprint","INTERSECT",VERTEX,{"derivedFrom":[subQ1,subQ3]});Q7=makeQuery(id+"F1.imprint","IMPRINT",FACE,{"disambiguationData":[TD([[makeQuery(id+"F1.imprint","IMPRINT",EDGE,{"disambiguationData":[TD([[subQ4,1.0]])],"derivedFrom":subQ3}),1.0]])]});}
            var Q8;
            {var subQ3=sQuery(id+"F1.wireOp",EDGE,"6cIBHAnO-3Gdr-gs2R-q8mb-qejxkHO2rhEE");var subQ5=sQuery(id+"F1.wireOp",EDGE,"E14");var subQ6=makeQuery(id+"F1.imprint","INTERSECT",VERTEX,{"derivedFrom":[subQ5,subQ3]});Q8=makeQuery(id+"F1.imprint","IMPRINT",FACE,{"disambiguationData":[TD([[makeQuery(id+"F1.imprint","IMPRINT",EDGE,{"disambiguationData":[TD([[subQ6,-1.0]])],"derivedFrom":subQ5}),1.0]])]});}
            var Q9;
            {var subQ0=sQuery(id+"F1.wireOp",EDGE,"E22");var subQ1=sQuery(id+"F1.wireOp",EDGE,"E14");var subQ2=makeQuery(id+"F1.imprint","INTERSECT",VERTEX,{"derivedFrom":[subQ1,subQ0]});Q9=makeQuery(id+"F1.imprint","IMPRINT",FACE,{"disambiguationData":[TD([[makeQuery(id+"F1.imprint","IMPRINT",EDGE,{"disambiguationData":[TD([[subQ2,-1.0]])],"derivedFrom":subQ1}),1.0]])]});}
            var Q10;
            {var subQ3=sQuery(id+"F1.wireOp",EDGE,"1679b663-5bbc-411f-b373-dbe6ce103e45.trimOffspring");var subQ5=sQuery(id+"F1.wireOp",EDGE,"E14");var subQ7=makeQuery(id+"F1.imprint","INTERSECT",VERTEX,{"disambiguationData":[OD(1.0)],"derivedFrom":[subQ5,subQ3]});Q10=makeQuery(id+"F1.imprint","IMPRINT",FACE,{"disambiguationData":[TD([[makeQuery(id+"F1.imprint","IMPRINT",EDGE,{"disambiguationData":[TD([[subQ7,-1.0]])],"derivedFrom":subQ5}),1.0]])]});}
            var Q11;
            {var subQ3=sQuery(id+"F1.wireOp",EDGE,"8l5Dcz2D-qY2G-ceuh-glFK-kLwJx8DI5XpU");var subQ5=sQuery(id+"F1.wireOp",EDGE,"E14");var subQ7=makeQuery(id+"F1.imprint","INTERSECT",VERTEX,{"derivedFrom":[subQ5,subQ3]});Q11=makeQuery(id+"F1.imprint","IMPRINT",FACE,{"disambiguationData":[TD([[makeQuery(id+"F1.imprint","IMPRINT",EDGE,{"disambiguationData":[TD([[subQ7,-1.0]])],"derivedFrom":subQ5}),1.0]])]});}
            var Q12;
            {var subQ0=sQuery(id+"F1.wireOp",EDGE,"n5LII22h-w08l-qE72-yfr9-18N67uZxNTdQ");var subQ1=sQuery(id+"F1.wireOp",EDGE,"E3");var subQ2=makeQuery(id+"F1.imprint","INTERSECT",VERTEX,{"derivedFrom":[subQ1,subQ0]});Q12=makeQuery(id+"F1.imprint","IMPRINT",FACE,{"disambiguationData":[TD([[makeQuery(id+"F1.imprint","IMPRINT",EDGE,{"disambiguationData":[TD([[subQ2,-1.0]])],"derivedFrom":subQ1}),-1.0]])]});}
            var Q13;
            {var subQ0=sQuery(id+"F1.wireOp",EDGE,"KU0cdiGB-8eOj-Trs3-v5YD-3LzdnCRRimhK");var subQ1=sQuery(id+"F1.wireOp",EDGE,"E3");var subQ2=makeQuery(id+"F1.imprint","INTERSECT",VERTEX,{"derivedFrom":[subQ1,subQ0]});Q13=makeQuery(id+"F1.imprint","IMPRINT",FACE,{"disambiguationData":[TD([[makeQuery(id+"F1.imprint","IMPRINT",EDGE,{"disambiguationData":[TD([[subQ2,-1.0]])],"derivedFrom":subQ1}),-1.0]])]});}
            var Q14;
            {var subQ0=sQuery(id+"F1.wireOp",EDGE,"SVIod6WE-LFFt-Ms97-owyS-8ShU65W6W8it");var subQ1=sQuery(id+"F1.wireOp",EDGE,"E3");var subQ2=makeQuery(id+"F1.imprint","INTERSECT",VERTEX,{"derivedFrom":[subQ1,subQ0]});Q14=makeQuery(id+"F1.imprint","IMPRINT",FACE,{"disambiguationData":[TD([[makeQuery(id+"F1.imprint","IMPRINT",EDGE,{"disambiguationData":[TD([[subQ2,-1.0]])],"derivedFrom":subQ1}),-1.0]])]});}
            var Q15;
            {var subQ0=sQuery(id+"F1.wireOp",EDGE,"SVIod6WE-LFFt-Ms97-owyS-8ShU65W6W8it");var subQ1=sQuery(id+"F1.wireOp",EDGE,"E3");var subQ2=makeQuery(id+"F1.imprint","INTERSECT",VERTEX,{"derivedFrom":[subQ1,subQ0]});Q15=makeQuery(id+"F1.imprint","IMPRINT",FACE,{"disambiguationData":[TD([[makeQuery(id+"F1.imprint","IMPRINT",EDGE,{"disambiguationData":[TD([[subQ2,1.0]])],"derivedFrom":subQ1}),-1.0]])]});}
            var Q16;
            {var subQ0=sQuery(id+"F1.wireOp",EDGE,"E24");var subQ1=sQuery(id+"F1.wireOp",EDGE,"E3");var subQ2=makeQuery(id+"F1.imprint","INTERSECT",VERTEX,{"derivedFrom":[subQ1,subQ0]});Q16=makeQuery(id+"F1.imprint","IMPRINT",FACE,{"disambiguationData":[TD([[makeQuery(id+"F1.imprint","IMPRINT",EDGE,{"disambiguationData":[TD([[subQ2,-1.0]])],"derivedFrom":subQ1}),-1.0]])]});}
            var Q17;
            {var subQ0=sQuery(id+"F1.wireOp",EDGE,"E23");var subQ1=sQuery(id+"F1.wireOp",EDGE,"E3");var subQ2=makeQuery(id+"F1.imprint","INTERSECT",VERTEX,{"derivedFrom":[subQ1,subQ0]});Q17=makeQuery(id+"F1.imprint","IMPRINT",FACE,{"disambiguationData":[TD([[makeQuery(id+"F1.imprint","IMPRINT",EDGE,{"disambiguationData":[TD([[subQ2,-1.0]])],"derivedFrom":subQ1}),-1.0]])]});}
            var Q18;
            {var subQ1=sQuery(id+"F1.wireOp",EDGE,"E27");var subQ3=sQuery(id+"F1.wireOp",EDGE,"E3");var subQ4=makeQuery(id+"F1.imprint","INTERSECT",VERTEX,{"derivedFrom":[subQ3,subQ1]});Q18=makeQuery(id+"F1.imprint","IMPRINT",FACE,{"disambiguationData":[TD([[makeQuery(id+"F1.imprint","IMPRINT",EDGE,{"disambiguationData":[TD([[subQ4,-1.0]])],"derivedFrom":subQ3}),-1.0]])]});}
            var Q19;
            {var subQ0=sQuery(id+"F1.wireOp",EDGE,"E30");var subQ1=sQuery(id+"F1.wireOp",EDGE,"E3");var subQ2=makeQuery(id+"F1.imprint","INTERSECT",VERTEX,{"derivedFrom":[subQ1,subQ0]});Q19=makeQuery(id+"F1.imprint","IMPRINT",FACE,{"disambiguationData":[TD([[makeQuery(id+"F1.imprint","IMPRINT",EDGE,{"disambiguationData":[TD([[subQ2,-1.0]])],"derivedFrom":subQ1}),-1.0]])]});}
            var Q20;
            {var subQ0=sQuery(id+"F1.wireOp",EDGE,"E25");var subQ7=sQuery(id+"F1.wireOp",EDGE,"E3");var subQ8=makeQuery(id+"F1.imprint","INTERSECT",VERTEX,{"derivedFrom":[subQ7,subQ0]});Q20=makeQuery(id+"F1.imprint","IMPRINT",FACE,{"disambiguationData":[TD([[makeQuery(id+"F1.imprint","IMPRINT",EDGE,{"disambiguationData":[TD([[subQ8,-1.0]])],"derivedFrom":subQ7}),-1.0]])]});}
            extrude(context, id + "F5", {"entities" : qUnion([Q0, Q1, Q2, Q3, Q4, Q5, Q6, Q7, Q8, Q9, Q10, Q11, Q12, Q13, Q14, Q15, Q16, Q17, Q18, Q19, Q20]), "operationType" : NewBodyOperationType.ADD, "depth" : 50.8 * mm});
        }
        {
            var Q0;
            {var subQ5=sQuery(id+"F1.wireOp",EDGE,"E12");Q0=makeQuery(id+"F1.imprint","IMPRINT",FACE,{"disambiguationData":[TD([[makeQuery(id+"F1.imprint","IMPRINT",EDGE,{"derivedFrom":subQ5}),-1.0]])]});}
            var Q1;
            {var subQ0=sQuery(id+"F1.wireOp",EDGE,"E13");Q1=makeQuery(id+"F1.imprint","IMPRINT",FACE,{"disambiguationData":[TD([[makeQuery(id+"F1.imprint","IMPRINT",EDGE,{"derivedFrom":subQ0}),1.0]])]});}
            var Q2;
            {var subQ0=sQuery(id+"F1.wireOp",EDGE,"E4");var subQ1=sQuery(id+"F1.wireOp",EDGE,"E3");var subQ2=makeQuery(id+"F1.imprint","INTERSECT",VERTEX,{"derivedFrom":[subQ1,subQ0]});Q2=makeQuery(id+"F1.imprint","IMPRINT",FACE,{"disambiguationData":[TD([[makeQuery(id+"F1.imprint","IMPRINT",EDGE,{"disambiguationData":[TD([[subQ2,-1.0]])],"derivedFrom":subQ1}),-1.0]])]});}
            var Q3;
            {var subQ2=sQuery(id+"F1.wireOp",EDGE,"E12");Q3=makeQuery(id+"F1.imprint","IMPRINT",FACE,{"disambiguationData":[TD([[makeQuery(id+"F1.imprint","IMPRINT",EDGE,{"derivedFrom":subQ2}),1.0]])]});}
            var Q4;
            {var subQ0=sQuery(id+"F1.wireOp",EDGE,"E17");Q4=makeQuery(id+"F1.imprint","IMPRINT",FACE,{"disambiguationData":[TD([[makeQuery(id+"F1.imprint","IMPRINT",EDGE,{"derivedFrom":subQ0}),-1.0]])]});}
            var Q5;
            {var subQ0=sQuery(id+"F1.wireOp",EDGE,"E6");var subQ5=sQuery(id+"F1.wireOp",EDGE,"E14");var subQ6=makeQuery(id+"F1.imprint","INTERSECT",VERTEX,{"derivedFrom":[subQ0,subQ5]});Q5=makeQuery(id+"F1.imprint","IMPRINT",FACE,{"disambiguationData":[TD([[makeQuery(id+"F1.imprint","IMPRINT",EDGE,{"disambiguationData":[TD([[subQ6,1.0]])],"derivedFrom":subQ5}),1.0]])]});}
            var Q6;
            {var subQ0=sQuery(id+"F1.wireOp",EDGE,"E16.trimOffspring");Q6=makeQuery(id+"F1.imprint","IMPRINT",FACE,{"disambiguationData":[TD([[makeQuery(id+"F1.imprint","IMPRINT",EDGE,{"derivedFrom":subQ0}),1.0]])]});}
            var Q7;
            {var subQ2=sQuery(id+"F1.wireOp",EDGE,"E15.trimOffspring");Q7=makeQuery(id+"F1.imprint","IMPRINT",FACE,{"disambiguationData":[TD([[makeQuery(id+"F1.imprint","IMPRINT",EDGE,{"derivedFrom":subQ2}),1.0]])]});}
            var Q8;
            {var subQ5=sQuery(id+"F1.wireOp",EDGE,"E15.trimOffspring");Q8=makeQuery(id+"F1.imprint","IMPRINT",FACE,{"disambiguationData":[TD([[makeQuery(id+"F1.imprint","IMPRINT",EDGE,{"derivedFrom":subQ5}),-1.0]])]});}
            var Q9;
            {var subQ0=sQuery(id+"F1.wireOp",EDGE,"8l5Dcz2D-qY2G-ceuh-glFK-kLwJx8DI5XpU");var subQ3=sQuery(id+"F1.wireOp",EDGE,"E18");var subQ5=makeQuery(id+"F1.imprint","INTERSECT",VERTEX,{"derivedFrom":[subQ3,subQ0]});Q9=makeQuery(id+"F1.imprint","IMPRINT",FACE,{"disambiguationData":[TD([[makeQuery(id+"F1.imprint","IMPRINT",EDGE,{"disambiguationData":[TD([[subQ5,-1.0]])],"derivedFrom":subQ3}),-1.0]])]});}
            var Q10;
            {var subQ1=sQuery(id+"F1.wireOp",EDGE,"E21");var subQ5=sQuery(id+"F1.wireOp",EDGE,"E18");var subQ6=makeQuery(id+"F1.imprint","INTERSECT",VERTEX,{"derivedFrom":[subQ5,subQ1]});Q10=makeQuery(id+"F1.imprint","IMPRINT",FACE,{"disambiguationData":[TD([[makeQuery(id+"F1.imprint","IMPRINT",EDGE,{"disambiguationData":[TD([[subQ6,-1.0]])],"derivedFrom":subQ5}),-1.0]])]});}
            var Q11;
            {var subQ1=sQuery(id+"F1.wireOp",EDGE,"E19");var subQ7=sQuery(id+"F1.wireOp",EDGE,"E17");var subQ8=makeQuery(id+"F1.imprint","INTERSECT",VERTEX,{"derivedFrom":[subQ7,subQ1]});Q11=makeQuery(id+"F1.imprint","IMPRINT",FACE,{"disambiguationData":[TD([[makeQuery(id+"F1.imprint","IMPRINT",EDGE,{"disambiguationData":[TD([[subQ8,-1.0]])],"derivedFrom":subQ7}),-1.0]])]});}
            var Q12;
            {var subQ3=sQuery(id+"F1.wireOp",EDGE,"E17");var subQ9=sQuery(id+"F1.wireOp",EDGE,"E22");var subQ10=makeQuery(id+"F1.imprint","INTERSECT",VERTEX,{"derivedFrom":[subQ3,subQ9]});Q12=makeQuery(id+"F1.imprint","IMPRINT",FACE,{"disambiguationData":[TD([[makeQuery(id+"F1.imprint","IMPRINT",EDGE,{"disambiguationData":[TD([[subQ10,-1.0]])],"derivedFrom":subQ3}),-1.0]])]});}
            var Q13;
            {var subQ0=sQuery(id+"F1.wireOp",EDGE,"E22");var subQ1=sQuery(id+"F1.wireOp",EDGE,"E17");var subQ2=makeQuery(id+"F1.imprint","INTERSECT",VERTEX,{"derivedFrom":[subQ1,subQ0]});Q13=makeQuery(id+"F1.imprint","IMPRINT",FACE,{"disambiguationData":[TD([[makeQuery(id+"F1.imprint","IMPRINT",EDGE,{"disambiguationData":[TD([[subQ2,1.0]])],"derivedFrom":subQ0}),1.0]])]});}
            var Q14;
            {var subQ3=sQuery(id+"F1.wireOp",EDGE,"E17");var subQ11=sQuery(id+"F1.wireOp",EDGE,"E23");var subQ12=makeQuery(id+"F1.imprint","INTERSECT",VERTEX,{"derivedFrom":[subQ3,subQ11]});Q14=makeQuery(id+"F1.imprint","IMPRINT",FACE,{"disambiguationData":[TD([[makeQuery(id+"F1.imprint","IMPRINT",EDGE,{"disambiguationData":[TD([[subQ12,-1.0]])],"derivedFrom":subQ3}),-1.0]])]});}
            var Q15;
            {var subQ0=sQuery(id+"F1.wireOp",EDGE,"E20");var subQ1=sQuery(id+"F1.wireOp",EDGE,"E18");var subQ2=makeQuery(id+"F1.imprint","INTERSECT",VERTEX,{"derivedFrom":[subQ1,subQ0]});Q15=makeQuery(id+"F1.imprint","IMPRINT",FACE,{"disambiguationData":[TD([[makeQuery(id+"F1.imprint","IMPRINT",EDGE,{"disambiguationData":[TD([[subQ2,1.0]])],"derivedFrom":subQ0}),1.0]])]});}
            var Q16;
            {var subQ0=sQuery(id+"F1.wireOp",EDGE,"E18");var subQ3=sQuery(id+"F1.wireOp",EDGE,"E23");var subQ4=makeQuery(id+"F1.imprint","INTERSECT",VERTEX,{"derivedFrom":[subQ0,subQ3]});Q16=makeQuery(id+"F1.imprint","IMPRINT",FACE,{"disambiguationData":[TD([[makeQuery(id+"F1.imprint","IMPRINT",EDGE,{"disambiguationData":[TD([[subQ4,1.0]])],"derivedFrom":subQ3}),-1.0]])]});}
            var Q17;
            {var subQ0=sQuery(id+"F1.wireOp",EDGE,"E24");var subQ3=sQuery(id+"F1.wireOp",EDGE,"E25");var subQ4=makeQuery(id+"F1.imprint","INTERSECT",VERTEX,{"derivedFrom":[subQ0,subQ3]});Q17=makeQuery(id+"F1.imprint","IMPRINT",FACE,{"disambiguationData":[TD([[makeQuery(id+"F1.imprint","IMPRINT",EDGE,{"disambiguationData":[TD([[subQ4,1.0]])],"derivedFrom":subQ0}),1.0]])]});}
            var Q18;
            {var subQ0=sQuery(id+"F1.wireOp",EDGE,"E20");var subQ1=sQuery(id+"F1.wireOp",EDGE,"E19");var subQ2=makeQuery(id+"F1.imprint","INTERSECT",VERTEX,{"derivedFrom":[subQ1,subQ0]});Q18=makeQuery(id+"F1.imprint","IMPRINT",FACE,{"disambiguationData":[TD([[makeQuery(id+"F1.imprint","IMPRINT",EDGE,{"disambiguationData":[TD([[subQ2,-1.0]])],"derivedFrom":subQ1}),-1.0]])]});}
            var Q19;
            {var subQ0=sQuery(id+"F1.wireOp",EDGE,"E22");var subQ1=sQuery(id+"F1.wireOp",EDGE,"E21");var subQ2=makeQuery(id+"F1.imprint","INTERSECT",VERTEX,{"derivedFrom":[subQ1,subQ0]});Q19=makeQuery(id+"F1.imprint","IMPRINT",FACE,{"disambiguationData":[TD([[makeQuery(id+"F1.imprint","IMPRINT",EDGE,{"disambiguationData":[TD([[subQ2,-1.0]])],"derivedFrom":subQ1}),-1.0]])]});}
            var Q20;
            {var subQ0=sQuery(id+"F1.wireOp",EDGE,"E25");var subQ1=sQuery(id+"F1.wireOp",EDGE,"E17");var subQ2=makeQuery(id+"F1.imprint","INTERSECT",VERTEX,{"derivedFrom":[subQ1,subQ0]});Q20=makeQuery(id+"F1.imprint","IMPRINT",FACE,{"disambiguationData":[TD([[makeQuery(id+"F1.imprint","IMPRINT",EDGE,{"disambiguationData":[TD([[subQ2,-1.0]])],"derivedFrom":subQ1}),-1.0]])]});}
            var Q21;
            {var subQ0=sQuery(id+"F1.wireOp",EDGE,"E26");var subQ1=sQuery(id+"F1.wireOp",EDGE,"E18");var subQ2=makeQuery(id+"F1.imprint","INTERSECT",VERTEX,{"derivedFrom":[subQ1,subQ0]});Q21=makeQuery(id+"F1.imprint","IMPRINT",FACE,{"disambiguationData":[TD([[makeQuery(id+"F1.imprint","IMPRINT",EDGE,{"disambiguationData":[TD([[subQ2,-1.0]])],"derivedFrom":subQ1}),-1.0]])]});}
            var Q22;
            {var subQ0=sQuery(id+"F1.wireOp",EDGE,"E20");var subQ1=sQuery(id+"F1.wireOp",EDGE,"E18");var subQ2=makeQuery(id+"F1.imprint","INTERSECT",VERTEX,{"derivedFrom":[subQ1,subQ0]});Q22=makeQuery(id+"F1.imprint","IMPRINT",FACE,{"disambiguationData":[TD([[makeQuery(id+"F1.imprint","IMPRINT",EDGE,{"disambiguationData":[TD([[subQ2,-1.0]])],"derivedFrom":subQ1}),-1.0]])]});}
            extrude(context, id + "F6", {"entities" : qUnion([Q0, Q1, Q2, Q3, Q4, Q5, Q6, Q7, Q8, Q9, Q10, Q11, Q12, Q13, Q14, Q15, Q16, Q17, Q18, Q19, Q20, Q21, Q22]), "operationType" : NewBodyOperationType.ADD, "depth" : 50.8 * mm});
        }
        {
            var Q0;
            {var subQ0=sQuery(id+"F1.wireOp",EDGE,"SVIod6WE-LFFt-Ms97-owyS-8ShU65W6W8it");var subQ1=sQuery(id+"F1.wireOp",EDGE,"E3");var subQ2=makeQuery(id+"F1.imprint","INTERSECT",VERTEX,{"derivedFrom":[subQ1,subQ0]});Q0=makeQuery(id+"F1.imprint","IMPRINT",FACE,{"disambiguationData":[TD([[makeQuery(id+"F1.imprint","IMPRINT",EDGE,{"disambiguationData":[TD([[subQ2,1.0]])],"derivedFrom":subQ1}),1.0]])]});}
            var Q1;
            {var subQ1=sQuery(id+"F1.wireOp",EDGE,"E3");var subQ3=sQuery(id+"F1.wireOp",EDGE,"I2xWRYXB-6D2N-iSpQ-MyaY-Cu2MAQN8JGNk");var subQ4=makeQuery(id+"F1.imprint","INTERSECT",VERTEX,{"derivedFrom":[subQ1,subQ3]});Q1=makeQuery(id+"F1.imprint","IMPRINT",FACE,{"disambiguationData":[TD([[makeQuery(id+"F1.imprint","IMPRINT",EDGE,{"disambiguationData":[TD([[subQ4,-1.0]])],"derivedFrom":subQ1}),1.0]])]});}
            var Q2;
            {var subQ0=sQuery(id+"F1.wireOp",EDGE,"n5LII22h-w08l-qE72-yfr9-18N67uZxNTdQ");var subQ1=sQuery(id+"F1.wireOp",EDGE,"E3");var subQ2=makeQuery(id+"F1.imprint","INTERSECT",VERTEX,{"derivedFrom":[subQ1,subQ0]});Q2=makeQuery(id+"F1.imprint","IMPRINT",FACE,{"disambiguationData":[TD([[makeQuery(id+"F1.imprint","IMPRINT",EDGE,{"disambiguationData":[TD([[subQ2,-1.0]])],"derivedFrom":subQ1}),1.0]])]});}
            var Q3;
            {var subQ0=sQuery(id+"F1.wireOp",EDGE,"E22");var subQ1=sQuery(id+"F1.wireOp",EDGE,"E3");var subQ2=makeQuery(id+"F1.imprint","INTERSECT",VERTEX,{"derivedFrom":[subQ1,subQ0]});Q3=makeQuery(id+"F1.imprint","IMPRINT",FACE,{"disambiguationData":[TD([[makeQuery(id+"F1.imprint","IMPRINT",EDGE,{"disambiguationData":[TD([[subQ2,-1.0]])],"derivedFrom":subQ1}),1.0]])]});}
            var Q4;
            {var subQ0=sQuery(id+"F1.wireOp",EDGE,"E27");var subQ1=sQuery(id+"F1.wireOp",EDGE,"E3");var subQ2=makeQuery(id+"F1.imprint","INTERSECT",VERTEX,{"derivedFrom":[subQ1,subQ0]});Q4=makeQuery(id+"F1.imprint","IMPRINT",FACE,{"disambiguationData":[TD([[makeQuery(id+"F1.imprint","IMPRINT",EDGE,{"disambiguationData":[TD([[subQ2,-1.0]])],"derivedFrom":subQ1}),1.0]])]});}
            var Q5;
            {var subQ0=sQuery(id+"F1.wireOp",EDGE,"E19");var subQ1=sQuery(id+"F1.wireOp",EDGE,"E0");var subQ2=makeQuery(id+"F1.imprint","INTERSECT",VERTEX,{"derivedFrom":[subQ1,subQ0]});Q5=makeQuery(id+"F1.imprint","IMPRINT",FACE,{"disambiguationData":[TD([[makeQuery(id+"F1.imprint","IMPRINT",EDGE,{"disambiguationData":[TD([[subQ2,-1.0]])],"derivedFrom":subQ1}),1.0]])]});}
            var Q6;
            {var subQ0=sQuery(id+"F1.wireOp",EDGE,"E19");var subQ1=sQuery(id+"F1.wireOp",EDGE,"E10.trimOffspring");var subQ2=makeQuery(id+"F1.imprint","INTERSECT",VERTEX,{"derivedFrom":[subQ1,subQ0]});Q6=makeQuery(id+"F1.imprint","IMPRINT",FACE,{"disambiguationData":[TD([[makeQuery(id+"F1.imprint","IMPRINT",EDGE,{"disambiguationData":[TD([[subQ2,-1.0]])],"derivedFrom":subQ1}),-1.0]])]});}
            var Q7;
            {var subQ0=sQuery(id+"F1.wireOp",EDGE,"E19");var subQ1=sQuery(id+"F1.wireOp",EDGE,"E10.trimOffspring");var subQ2=makeQuery(id+"F1.imprint","INTERSECT",VERTEX,{"derivedFrom":[subQ1,subQ0]});Q7=makeQuery(id+"F1.imprint","IMPRINT",FACE,{"disambiguationData":[TD([[makeQuery(id+"F1.imprint","IMPRINT",EDGE,{"disambiguationData":[TD([[subQ2,-1.0]])],"derivedFrom":subQ1}),1.0]])]});}
            var Q8;
            {var subQ0=sQuery(id+"F1.wireOp",EDGE,"E19");var subQ1=sQuery(id+"F1.wireOp",EDGE,"E3");var subQ2=makeQuery(id+"F1.imprint","INTERSECT",VERTEX,{"derivedFrom":[subQ1,subQ0]});Q8=makeQuery(id+"F1.imprint","IMPRINT",FACE,{"disambiguationData":[TD([[makeQuery(id+"F1.imprint","IMPRINT",EDGE,{"disambiguationData":[TD([[subQ2,-1.0]])],"derivedFrom":subQ1}),-1.0]])]});}
            var Q9;
            {var subQ1=sQuery(id+"F1.wireOp",EDGE,"E19");var subQ6=sQuery(id+"F1.wireOp",EDGE,"E3");var subQ9=makeQuery(id+"F1.imprint","INTERSECT",VERTEX,{"derivedFrom":[subQ6,subQ1]});Q9=makeQuery(id+"F1.imprint","IMPRINT",FACE,{"disambiguationData":[TD([[makeQuery(id+"F1.imprint","IMPRINT",EDGE,{"disambiguationData":[TD([[subQ9,-1.0]])],"derivedFrom":subQ6}),1.0]])]});}
            var Q10;
            {var subQ0=sQuery(id+"F1.wireOp",EDGE,"E22");var subQ1=sQuery(id+"F1.wireOp",EDGE,"E17");var subQ2=makeQuery(id+"F1.imprint","INTERSECT",VERTEX,{"derivedFrom":[subQ1,subQ0]});Q10=makeQuery(id+"F1.imprint","IMPRINT",FACE,{"disambiguationData":[TD([[makeQuery(id+"F1.imprint","IMPRINT",EDGE,{"disambiguationData":[TD([[subQ2,-1.0]])],"derivedFrom":subQ1}),-1.0]])]});}
            var Q11;
            {var subQ1=sQuery(id+"F1.wireOp",EDGE,"E3");var subQ7=sQuery(id+"F1.wireOp",EDGE,"E20");var subQ9=makeQuery(id+"F1.imprint","INTERSECT",VERTEX,{"derivedFrom":[subQ1,subQ7]});Q11=makeQuery(id+"F1.imprint","IMPRINT",FACE,{"disambiguationData":[TD([[makeQuery(id+"F1.imprint","IMPRINT",EDGE,{"disambiguationData":[TD([[subQ9,1.0]])],"derivedFrom":subQ1}),1.0]])]});}
            var Q12;
            {var subQ0=sQuery(id+"F1.wireOp",EDGE,"E20");var subQ1=sQuery(id+"F1.wireOp",EDGE,"E3");var subQ2=makeQuery(id+"F1.imprint","INTERSECT",VERTEX,{"derivedFrom":[subQ1,subQ0]});Q12=makeQuery(id+"F1.imprint","IMPRINT",FACE,{"disambiguationData":[TD([[makeQuery(id+"F1.imprint","IMPRINT",EDGE,{"disambiguationData":[TD([[subQ2,1.0]])],"derivedFrom":subQ1}),-1.0]])]});}
            var Q13;
            {var subQ0=sQuery(id+"F1.wireOp",EDGE,"E21");var subQ1=sQuery(id+"F1.wireOp",EDGE,"E2");var subQ2=makeQuery(id+"F1.imprint","INTERSECT",VERTEX,{"derivedFrom":[subQ1,subQ0]});Q13=makeQuery(id+"F1.imprint","IMPRINT",FACE,{"disambiguationData":[TD([[makeQuery(id+"F1.imprint","IMPRINT",EDGE,{"disambiguationData":[TD([[subQ2,-1.0]])],"derivedFrom":subQ1}),1.0]])]});}
            var Q14;
            {var subQ0=sQuery(id+"F1.wireOp",EDGE,"E20");var subQ1=sQuery(id+"F1.wireOp",EDGE,"E0");var subQ2=makeQuery(id+"F1.imprint","INTERSECT",VERTEX,{"derivedFrom":[subQ1,subQ0]});Q14=makeQuery(id+"F1.imprint","IMPRINT",FACE,{"disambiguationData":[TD([[makeQuery(id+"F1.imprint","IMPRINT",EDGE,{"disambiguationData":[TD([[subQ2,1.0]])],"derivedFrom":subQ1}),1.0]])]});}
            var Q15;
            {var subQ0=sQuery(id+"F1.wireOp",EDGE,"E22");var subQ1=sQuery(id+"F1.wireOp",EDGE,"E17");var subQ2=makeQuery(id+"F1.imprint","INTERSECT",VERTEX,{"derivedFrom":[subQ1,subQ0]});Q15=makeQuery(id+"F1.imprint","IMPRINT",FACE,{"disambiguationData":[TD([[makeQuery(id+"F1.imprint","IMPRINT",EDGE,{"disambiguationData":[TD([[subQ2,-1.0]])],"derivedFrom":subQ1}),1.0]])]});}
            var Q16;
            {var subQ0=sQuery(id+"F1.wireOp",EDGE,"E20");var subQ1=sQuery(id+"F1.wireOp",EDGE,"E18");var subQ2=makeQuery(id+"F1.imprint","INTERSECT",VERTEX,{"derivedFrom":[subQ1,subQ0]});Q16=makeQuery(id+"F1.imprint","IMPRINT",FACE,{"disambiguationData":[TD([[makeQuery(id+"F1.imprint","IMPRINT",EDGE,{"disambiguationData":[TD([[subQ2,-1.0]])],"derivedFrom":subQ1}),1.0]])]});}
            var Q17;
            {var subQ0=sQuery(id+"F1.wireOp",EDGE,"E23");var subQ1=sQuery(id+"F1.wireOp",EDGE,"E17");var subQ2=makeQuery(id+"F1.imprint","INTERSECT",VERTEX,{"derivedFrom":[subQ1,subQ0]});Q17=makeQuery(id+"F1.imprint","IMPRINT",FACE,{"disambiguationData":[TD([[makeQuery(id+"F1.imprint","IMPRINT",EDGE,{"disambiguationData":[TD([[subQ2,-1.0]])],"derivedFrom":subQ1}),1.0]])]});}
            var Q18;
            {var subQ0=sQuery(id+"F1.wireOp",EDGE,"E24");var subQ1=sQuery(id+"F1.wireOp",EDGE,"E18");var subQ2=makeQuery(id+"F1.imprint","INTERSECT",VERTEX,{"derivedFrom":[subQ1,subQ0]});Q18=makeQuery(id+"F1.imprint","IMPRINT",FACE,{"disambiguationData":[TD([[makeQuery(id+"F1.imprint","IMPRINT",EDGE,{"disambiguationData":[TD([[subQ2,-1.0]])],"derivedFrom":subQ1}),1.0]])]});}
            var Q19;
            {var subQ0=sQuery(id+"F1.wireOp",EDGE,"KU0cdiGB-8eOj-Trs3-v5YD-3LzdnCRRimhK");var subQ3=sQuery(id+"F1.wireOp",EDGE,"E3");var subQ4=makeQuery(id+"F1.imprint","INTERSECT",VERTEX,{"derivedFrom":[subQ3,subQ0]});Q19=makeQuery(id+"F1.imprint","IMPRINT",FACE,{"disambiguationData":[TD([[makeQuery(id+"F1.imprint","IMPRINT",EDGE,{"disambiguationData":[TD([[subQ4,-1.0]])],"derivedFrom":subQ3}),1.0]])]});}
            var Q20;
            {var subQ0=sQuery(id+"F1.wireOp",EDGE,"E25");var subQ1=sQuery(id+"F1.wireOp",EDGE,"E17");var subQ2=makeQuery(id+"F1.imprint","INTERSECT",VERTEX,{"derivedFrom":[subQ1,subQ0]});Q20=makeQuery(id+"F1.imprint","IMPRINT",FACE,{"disambiguationData":[TD([[makeQuery(id+"F1.imprint","IMPRINT",EDGE,{"disambiguationData":[TD([[subQ2,-1.0]])],"derivedFrom":subQ1}),1.0]])]});}
            var Q21;
            {var subQ0=sQuery(id+"F1.wireOp",EDGE,"E26");var subQ1=sQuery(id+"F1.wireOp",EDGE,"E18");var subQ2=makeQuery(id+"F1.imprint","INTERSECT",VERTEX,{"derivedFrom":[subQ1,subQ0]});Q21=makeQuery(id+"F1.imprint","IMPRINT",FACE,{"disambiguationData":[TD([[makeQuery(id+"F1.imprint","IMPRINT",EDGE,{"disambiguationData":[TD([[subQ2,-1.0]])],"derivedFrom":subQ1}),1.0]])]});}
            var Q22;
            {var subQ3=sQuery(id+"F1.wireOp",EDGE,"E25");var subQ5=sQuery(id+"F1.wireOp",EDGE,"E3");var subQ6=makeQuery(id+"F1.imprint","INTERSECT",VERTEX,{"derivedFrom":[subQ5,subQ3]});Q22=makeQuery(id+"F1.imprint","IMPRINT",FACE,{"disambiguationData":[TD([[makeQuery(id+"F1.imprint","IMPRINT",EDGE,{"disambiguationData":[TD([[subQ6,-1.0]])],"derivedFrom":subQ5}),1.0]])]});}
            var Q23;
            {var subQ0=sQuery(id+"F1.wireOp",EDGE,"E27");var subQ1=sQuery(id+"F1.wireOp",EDGE,"E3");var subQ2=makeQuery(id+"F1.imprint","INTERSECT",VERTEX,{"derivedFrom":[subQ1,subQ0]});Q23=makeQuery(id+"F1.imprint","IMPRINT",FACE,{"disambiguationData":[TD([[makeQuery(id+"F1.imprint","IMPRINT",EDGE,{"disambiguationData":[TD([[subQ2,-1.0]])],"derivedFrom":subQ1}),1.0]])]});}
            var Q24;
            {var subQ0=sQuery(id+"F1.wireOp",EDGE,"SVIod6WE-LFFt-Ms97-owyS-8ShU65W6W8it");var subQ7=sQuery(id+"F1.wireOp",EDGE,"E3");var subQ9=makeQuery(id+"F1.imprint","INTERSECT",VERTEX,{"derivedFrom":[subQ7,subQ0]});Q24=makeQuery(id+"F1.imprint","IMPRINT",FACE,{"disambiguationData":[TD([[makeQuery(id+"F1.imprint","IMPRINT",EDGE,{"disambiguationData":[TD([[subQ9,-1.0]])],"derivedFrom":subQ7}),1.0]])]});}
            var Q25;
            {var subQ0=sQuery(id+"F1.wireOp",EDGE,"E24");var subQ1=sQuery(id+"F1.wireOp",EDGE,"E3");var subQ2=makeQuery(id+"F1.imprint","INTERSECT",VERTEX,{"derivedFrom":[subQ1,subQ0]});Q25=makeQuery(id+"F1.imprint","IMPRINT",FACE,{"disambiguationData":[TD([[makeQuery(id+"F1.imprint","IMPRINT",EDGE,{"disambiguationData":[TD([[subQ2,-1.0]])],"derivedFrom":subQ1}),1.0]])]});}
            var Q26;
            {var subQ0=sQuery(id+"F1.wireOp",EDGE,"E23");var subQ1=sQuery(id+"F1.wireOp",EDGE,"E3");var subQ2=makeQuery(id+"F1.imprint","INTERSECT",VERTEX,{"derivedFrom":[subQ1,subQ0]});Q26=makeQuery(id+"F1.imprint","IMPRINT",FACE,{"disambiguationData":[TD([[makeQuery(id+"F1.imprint","IMPRINT",EDGE,{"disambiguationData":[TD([[subQ2,-1.0]])],"derivedFrom":subQ1}),1.0]])]});}
            var Q27;
            {var subQ1=sQuery(id+"F1.wireOp",EDGE,"E3");var subQ3=sQuery(id+"F1.wireOp",EDGE,"E23");var subQ4=makeQuery(id+"F1.imprint","INTERSECT",VERTEX,{"derivedFrom":[subQ1,subQ3]});Q27=makeQuery(id+"F1.imprint","IMPRINT",FACE,{"disambiguationData":[TD([[makeQuery(id+"F1.imprint","IMPRINT",EDGE,{"disambiguationData":[TD([[subQ4,1.0]])],"derivedFrom":subQ3}),-1.0]])]});}
            var Q28;
            {var subQ1=sQuery(id+"F1.wireOp",EDGE,"E3");var subQ3=sQuery(id+"F1.wireOp",EDGE,"E26");var subQ4=makeQuery(id+"F1.imprint","INTERSECT",VERTEX,{"derivedFrom":[subQ1,subQ3]});Q28=makeQuery(id+"F1.imprint","IMPRINT",FACE,{"disambiguationData":[TD([[makeQuery(id+"F1.imprint","IMPRINT",EDGE,{"disambiguationData":[TD([[subQ4,1.0]])],"derivedFrom":subQ3}),1.0]])]});}
            var Q29;
            {var subQ1=sQuery(id+"F1.wireOp",EDGE,"E3");var subQ3=sQuery(id+"F1.wireOp",EDGE,"KU0cdiGB-8eOj-Trs3-v5YD-3LzdnCRRimhK");var subQ4=makeQuery(id+"F1.imprint","INTERSECT",VERTEX,{"derivedFrom":[subQ1,subQ3]});Q29=makeQuery(id+"F1.imprint","IMPRINT",FACE,{"disambiguationData":[TD([[makeQuery(id+"F1.imprint","IMPRINT",EDGE,{"disambiguationData":[TD([[subQ4,1.0]])],"derivedFrom":subQ1}),1.0]])]});}
            var Q30;
            {var subQ0=sQuery(id+"F1.wireOp",EDGE,"E27");var subQ1=sQuery(id+"F1.wireOp",EDGE,"E17");var subQ2=makeQuery(id+"F1.imprint","INTERSECT",VERTEX,{"derivedFrom":[subQ1,subQ0]});Q30=makeQuery(id+"F1.imprint","IMPRINT",FACE,{"disambiguationData":[TD([[makeQuery(id+"F1.imprint","IMPRINT",EDGE,{"disambiguationData":[TD([[subQ2,-1.0]])],"derivedFrom":subQ1}),1.0]])]});}
            var Q31;
            {var subQ5=sQuery(id+"F1.wireOp",EDGE,"E36");var subQ7=sQuery(id+"F1.wireOp",EDGE,"E3");var subQ9=makeQuery(id+"F1.imprint","INTERSECT",VERTEX,{"derivedFrom":[subQ7,subQ5]});Q31=makeQuery(id+"F1.imprint","IMPRINT",FACE,{"disambiguationData":[TD([[makeQuery(id+"F1.imprint","IMPRINT",EDGE,{"disambiguationData":[TD([[subQ9,-1.0]])],"derivedFrom":subQ7}),1.0]])]});}
            var Q32;
            {var subQ5=sQuery(id+"F1.wireOp",EDGE,"E35");var subQ7=sQuery(id+"F1.wireOp",EDGE,"E3");var subQ8=makeQuery(id+"F1.imprint","INTERSECT",VERTEX,{"derivedFrom":[subQ7,subQ5]});Q32=makeQuery(id+"F1.imprint","IMPRINT",FACE,{"disambiguationData":[TD([[makeQuery(id+"F1.imprint","IMPRINT",EDGE,{"disambiguationData":[TD([[subQ8,1.0]])],"derivedFrom":subQ7}),1.0]])]});}
            var Q33;
            {var subQ5=sQuery(id+"F1.wireOp",EDGE,"E32");var subQ7=sQuery(id+"F1.wireOp",EDGE,"E3");var subQ8=makeQuery(id+"F1.imprint","INTERSECT",VERTEX,{"derivedFrom":[subQ7,subQ5]});Q33=makeQuery(id+"F1.imprint","IMPRINT",FACE,{"disambiguationData":[TD([[makeQuery(id+"F1.imprint","IMPRINT",EDGE,{"disambiguationData":[TD([[subQ8,-1.0]])],"derivedFrom":subQ7}),1.0]])]});}
            var Q34;
            {var subQ0=sQuery(id+"F1.wireOp",EDGE,"18cd6810-feed-407b-96fd-876ede30ebc9.trimOffspring");Q34=makeQuery(id+"F1.imprint","IMPRINT",FACE,{"disambiguationData":[TD([[makeQuery(id+"F1.imprint","IMPRINT",EDGE,{"derivedFrom":subQ0}),1.0]])]});}
            var Q35;
            {var subQ0=sQuery(id+"F1.wireOp",EDGE,"E21");var subQ1=sQuery(id+"F1.wireOp",EDGE,"E2");var subQ2=makeQuery(id+"F1.imprint","INTERSECT",VERTEX,{"derivedFrom":[subQ1,subQ0]});Q35=makeQuery(id+"F1.imprint","IMPRINT",FACE,{"disambiguationData":[TD([[makeQuery(id+"F1.imprint","IMPRINT",EDGE,{"disambiguationData":[TD([[subQ2,-1.0]])],"derivedFrom":subQ1}),-1.0]])]});}
            extrude(context, id + "F7", {"entities" : qUnion([Q0, Q1, Q2, Q3, Q4, Q5, Q6, Q7, Q8, Q9, Q10, Q11, Q12, Q13, Q14, Q15, Q16, Q17, Q18, Q19, Q20, Q21, Q22, Q23, Q24, Q25, Q26, Q27, Q28, Q29, Q30, Q31, Q32, Q33, Q34, Q35]), "operationType" : NewBodyOperationType.ADD, "depth" : 50.8 * mm});
        }
        {
            var Q0;
            {var subQ0=sQuery(id+"F1.wireOp",EDGE,"E20");var subQ1=sQuery(id+"F1.wireOp",EDGE,"E19");var subQ2=sQuery(id+"F1.wireOp",EDGE,"E18");var subQ3=sQuery(id+"F1.wireOp",EDGE,"E17");var subQ4=sQuery(id+"F1.wireOp",EDGE,"E7");var subQ5=sQuery(id+"F1.wireOp",EDGE,"E6");var subQ6=sQuery(id+"F1.wireOp",EDGE,"E0");var subQ7=sQuery(id+"F1.wireOp",EDGE,"E14");var subQ8=sQuery(id+"F1.wireOp",EDGE,"E15.trimOffspring");var subQ9=sQuery(id+"F1.wireOp",EDGE,"E12");var subQ10=sQuery(id+"F1.wireOp",EDGE,"E11.trimOffspring");var subQ11=sQuery(id+"F1.wireOp",EDGE,"E1");var subQ12=sQuery(id+"F1.wireOp",EDGE,"E16.trimOffspring");var subQ13=sQuery(id+"F1.wireOp",EDGE,"E13");var subQ14=sQuery(id+"F1.wireOp",EDGE,"E10.trimOffspring");var subQ15=sQuery(id+"F1.wireOp",EDGE,"E2");var subQ16=sQuery(id+"F1.wireOp",EDGE,"E4");var subQ17=sQuery(id+"F1.wireOp",EDGE,"E5");var subQ18=sQuery(id+"F1.wireOp",EDGE,"E22");var subQ19=sQuery(id+"F1.wireOp",EDGE,"E21");Q0=makeQuery(id+"F7.boolean.opBoolean","SPLIT",FACE,{"disambiguationData":[TD([makeQuery(id+"F2.opExtrude","SWEPT_FACE",FACE,{"disambiguationData":[OSD([subQ6])]}),makeQuery(id+"F2.opExtrude","CAP_FACE",FACE,{"disambiguationData":[OSD([subQ6,subQ11,subQ10,subQ9,subQ8])],"isStart":false}),makeQuery(id+"F3.opExtrude","CAP_FACE",FACE,{"disambiguationData":[OSD([subQ11,subQ15,subQ14,subQ10,subQ9,subQ13,subQ8,subQ12])],"isStart":false}),makeQuery(id+"F3.opExtrude","SWEPT_FACE",FACE,{"disambiguationData":[OSD([subQ11,subQ10,subQ9,subQ8])]}),makeQuery(id+"F4.opExtrude","CAP_FACE",FACE,{"disambiguationData":[OSD([subQ15,subQ14,subQ13,subQ7,subQ12])],"isStart":false}),makeQuery(id+"F4.opExtrude","SWEPT_FACE",FACE,{"disambiguationData":[OSD([subQ15,subQ14,subQ13,subQ12])]}),makeQuery(id+"F5.opExtrude","CAP_FACE",FACE,{"disambiguationData":[OSD([sQuery(id+"F1.wireOp",EDGE,"E3"),subQ7])],"isStart":false}),makeQuery(id+"F5.opExtrude","SWEPT_FACE",FACE,{"disambiguationData":[OSD([subQ7])]}),makeQuery(id+"F6.opExtrude","SWEPT_FACE",FACE,{"disambiguationData":[OSD([subQ6]),TDD([makeQuery(id+"F1.imprint","IMPRINT",EDGE,{"disambiguationData":[TD([[makeQuery(id+"F1.imprint","INTERSECT",VERTEX,{"derivedFrom":[subQ6,subQ5]}),1.0]])],"derivedFrom":subQ6})])]}),makeQuery(id+"F6.opExtrude","CAP_FACE",FACE,{"disambiguationData":[OSD([subQ6,subQ5,subQ4,subQ3,subQ2,subQ1,subQ0])],"isStart":false}),makeQuery(id+"F6.opExtrude","SWEPT_FACE",FACE,{"disambiguationData":[OSD([subQ6]),TDD([makeQuery(id+"F1.imprint","IMPRINT",EDGE,{"disambiguationData":[TD([[makeQuery(id+"F1.imprint","INTERSECT",VERTEX,{"derivedFrom":[subQ6,subQ16]}),-1.0]])],"derivedFrom":subQ6})])]}),makeQuery(id+"F6.opExtrude","CAP_FACE",FACE,{"disambiguationData":[OSD([subQ6,subQ16,subQ17,subQ3,subQ2,subQ19,subQ18])],"isStart":false}),makeQuery(id+"F7.opExtrude","SWEPT_FACE",FACE,{"disambiguationData":[OSD([subQ6]),TDD([makeQuery(id+"F1.imprint","IMPRINT",EDGE,{"disambiguationData":[TD([[makeQuery(id+"F1.imprint","INTERSECT",VERTEX,{"derivedFrom":[subQ6,subQ1]}),-1.0]])],"derivedFrom":subQ6})])]}),makeQuery(id+"F7.opExtrude","CAP_FACE",FACE,{"disambiguationData":[OSD([subQ6,subQ1,subQ0,subQ19,subQ18])],"isStart":false}),makeQuery(id+"F7.opExtrude","SWEPT_FACE",FACE,{"disambiguationData":[OSD([subQ6]),TDD([makeQuery(id+"F1.imprint","IMPRINT",EDGE,{"disambiguationData":[TD([[makeQuery(id+"F1.imprint","INTERSECT",VERTEX,{"derivedFrom":[subQ6,subQ0]}),1.0]])],"derivedFrom":subQ6})])]})]),OD(1.0)],"derivedFrom":makeQuery(id+"F7.opExtrude","SWEPT_FACE",FACE,{"disambiguationData":[OSD([subQ19,subQ18])]})});}
            var sketch = newSketch(context, id + "F8", { "sketchPlane" : qUnion([Q0])});
            skLineSegment(sketch, "E42", {"start": v(-48.04, 12.7) * mm, "end": v(-7.66, 50.8) * mm});
            skLineSegment(sketch, "E43", {"start": v(-7.66, 50.8) * mm, "end": v(-7.66, 65.35) * mm});
            skLineSegment(sketch, "E44", {"start": v(-7.66, 65.35) * mm, "end": v(-55.92, 65.35) * mm});
            skLineSegment(sketch, "E45", {"start": v(-55.92, 65.35) * mm, "end": v(-55.51, 12.7) * mm});
            skLineSegment(sketch, "E46", {"start": v(-55.51, 12.7) * mm, "end": v(-48.04, 12.7) * mm});
            skSolve(sketch);
        }
        {
            var Q0;
            {var subQ0=sQuery(id+"F1.wireOp",EDGE,"E20");var subQ1=sQuery(id+"F1.wireOp",EDGE,"E19");var subQ2=sQuery(id+"F1.wireOp",EDGE,"E18");var subQ3=sQuery(id+"F1.wireOp",EDGE,"E17");var subQ4=sQuery(id+"F1.wireOp",EDGE,"E7");var subQ5=sQuery(id+"F1.wireOp",EDGE,"E6");var subQ6=sQuery(id+"F1.wireOp",EDGE,"E0");var subQ7=sQuery(id+"F1.wireOp",EDGE,"E14");var subQ8=sQuery(id+"F1.wireOp",EDGE,"E15.trimOffspring");var subQ9=sQuery(id+"F1.wireOp",EDGE,"E12");var subQ10=sQuery(id+"F1.wireOp",EDGE,"E11.trimOffspring");var subQ11=sQuery(id+"F1.wireOp",EDGE,"E1");var subQ12=sQuery(id+"F1.wireOp",EDGE,"E16.trimOffspring");var subQ13=sQuery(id+"F1.wireOp",EDGE,"E13");var subQ14=sQuery(id+"F1.wireOp",EDGE,"E10.trimOffspring");var subQ15=sQuery(id+"F1.wireOp",EDGE,"E2");var subQ16=sQuery(id+"F1.wireOp",EDGE,"E4");var subQ17=sQuery(id+"F1.wireOp",EDGE,"E5");var subQ18=sQuery(id+"F1.wireOp",EDGE,"E22");var subQ19=sQuery(id+"F1.wireOp",EDGE,"E21");Q0=makeQuery(id+"F7.boolean.opBoolean","SPLIT",FACE,{"disambiguationData":[TD([makeQuery(id+"F2.opExtrude","SWEPT_FACE",FACE,{"disambiguationData":[OSD([subQ6])]}),makeQuery(id+"F2.opExtrude","CAP_FACE",FACE,{"disambiguationData":[OSD([subQ6,subQ11,subQ10,subQ9,subQ8])],"isStart":false}),makeQuery(id+"F3.opExtrude","CAP_FACE",FACE,{"disambiguationData":[OSD([subQ11,subQ15,subQ14,subQ10,subQ9,subQ13,subQ8,subQ12])],"isStart":false}),makeQuery(id+"F3.opExtrude","SWEPT_FACE",FACE,{"disambiguationData":[OSD([subQ11,subQ10,subQ9,subQ8])]}),makeQuery(id+"F4.opExtrude","CAP_FACE",FACE,{"disambiguationData":[OSD([subQ15,subQ14,subQ13,subQ7,subQ12])],"isStart":false}),makeQuery(id+"F4.opExtrude","SWEPT_FACE",FACE,{"disambiguationData":[OSD([subQ15,subQ14,subQ13,subQ12])]}),makeQuery(id+"F5.opExtrude","CAP_FACE",FACE,{"disambiguationData":[OSD([sQuery(id+"F1.wireOp",EDGE,"E3"),subQ7])],"isStart":false}),makeQuery(id+"F5.opExtrude","SWEPT_FACE",FACE,{"disambiguationData":[OSD([subQ7])]}),makeQuery(id+"F6.opExtrude","SWEPT_FACE",FACE,{"disambiguationData":[OSD([subQ6]),TDD([makeQuery(id+"F1.imprint","IMPRINT",EDGE,{"disambiguationData":[TD([[makeQuery(id+"F1.imprint","INTERSECT",VERTEX,{"derivedFrom":[subQ6,subQ5]}),1.0]])],"derivedFrom":subQ6})])]}),makeQuery(id+"F6.opExtrude","CAP_FACE",FACE,{"disambiguationData":[OSD([subQ6,subQ5,subQ4,subQ3,subQ2,subQ1,subQ0])],"isStart":false}),makeQuery(id+"F6.opExtrude","SWEPT_FACE",FACE,{"disambiguationData":[OSD([subQ6]),TDD([makeQuery(id+"F1.imprint","IMPRINT",EDGE,{"disambiguationData":[TD([[makeQuery(id+"F1.imprint","INTERSECT",VERTEX,{"derivedFrom":[subQ6,subQ16]}),-1.0]])],"derivedFrom":subQ6})])]}),makeQuery(id+"F6.opExtrude","CAP_FACE",FACE,{"disambiguationData":[OSD([subQ6,subQ16,subQ17,subQ3,subQ2,subQ19,subQ18])],"isStart":false}),makeQuery(id+"F7.opExtrude","SWEPT_FACE",FACE,{"disambiguationData":[OSD([subQ6]),TDD([makeQuery(id+"F1.imprint","IMPRINT",EDGE,{"disambiguationData":[TD([[makeQuery(id+"F1.imprint","INTERSECT",VERTEX,{"derivedFrom":[subQ6,subQ1]}),-1.0]])],"derivedFrom":subQ6})])]}),makeQuery(id+"F7.opExtrude","CAP_FACE",FACE,{"disambiguationData":[OSD([subQ6,subQ1,subQ0,subQ19,subQ18])],"isStart":false}),makeQuery(id+"F7.opExtrude","SWEPT_FACE",FACE,{"disambiguationData":[OSD([subQ6]),TDD([makeQuery(id+"F1.imprint","IMPRINT",EDGE,{"disambiguationData":[TD([[makeQuery(id+"F1.imprint","INTERSECT",VERTEX,{"derivedFrom":[subQ6,subQ0]}),1.0]])],"derivedFrom":subQ6})])]})]),OD(0.0)],"derivedFrom":makeQuery(id+"F7.opExtrude","SWEPT_FACE",FACE,{"disambiguationData":[OSD([subQ19,subQ18])]})});}
            var sketch = newSketch(context, id + "F9", { "sketchPlane" : qUnion([Q0])});
            skLineSegment(sketch, "E47", {"start": v(47.9, 12.7) * mm, "end": v(7.67, 50.8) * mm});
            skLineSegment(sketch, "E48", {"start": v(7.67, 50.8) * mm, "end": v(7.67, 53.93) * mm});
            skLineSegment(sketch, "E49", {"start": v(7.67, 53.93) * mm, "end": v(55.4, 55.84) * mm});
            skLineSegment(sketch, "E50", {"start": v(55.4, 55.84) * mm, "end": v(55.4, 12.7) * mm});
            skLineSegment(sketch, "E51", {"start": v(55.4, 12.7) * mm, "end": v(47.9, 12.7) * mm});
            skSolve(sketch);
        }
        {
            var Q0;
            {var subQ0=sQuery(id+"F1.wireOp",EDGE,"E18");var subQ4=sQuery(id+"F1.wireOp",EDGE,"E0");var subQ15=sQuery(id+"F1.wireOp",EDGE,"E5");Q0=makeQuery(id+"F6.boolean.opBoolean","SPLIT",FACE,{"disambiguationData":[TD([makeQuery(id+"F2.opExtrude","SWEPT_FACE",FACE,{"disambiguationData":[OSD([subQ4])]})])],"derivedFrom":makeQuery(id+"F6.opExtrude","SWEPT_FACE",FACE,{"disambiguationData":[OSD([subQ15,subQ0])]})});}
            var sketch = newSketch(context, id + "F10", { "sketchPlane" : qUnion([Q0])});
            skLineSegment(sketch, "E52", {"start": v(-47.8, 12.7) * mm, "end": v(-7.66, 50.8) * mm});
            skLineSegment(sketch, "E53", {"start": v(-7.66, 50.8) * mm, "end": v(-7.66, 52.64) * mm});
            skLineSegment(sketch, "E54", {"start": v(-7.66, 52.64) * mm, "end": v(-57.52, 52.64) * mm});
            skLineSegment(sketch, "E55", {"start": v(-57.52, 52.64) * mm, "end": v(-58.6, 12.7) * mm});
            skLineSegment(sketch, "E56", {"start": v(-58.6, 12.7) * mm, "end": v(-47.8, 12.7) * mm});
            skSolve(sketch);
        }
        {
            var Q0;
            Q0=qSketchRegion(id+"F8",true);
            extrude(context, id + "F11", {"entities" : qUnion([Q0]), "operationType" : NewBodyOperationType.REMOVE, "oppositeDirection" : true, "depth" : 15.24 * mm});
        }
        {
            var Q0;
            Q0=qSketchRegion(id+"F9",true);
            extrude(context, id + "F12", {"entities" : qUnion([Q0]), "operationType" : NewBodyOperationType.REMOVE, "oppositeDirection" : true, "depth" : 15.24 * mm});
        }
        {
            var Q0;
            Q0=qSketchRegion(id+"F10",true);
            extrude(context, id + "F13", {"entities" : qUnion([Q0]), "operationType" : NewBodyOperationType.REMOVE, "oppositeDirection" : true, "depth" : 15.24 * mm});
        }
        {
            var Q0;
            {var subQ0=sQuery(id+"F1.wireOp",EDGE,"E17");var subQ1=sQuery(id+"F1.wireOp",EDGE,"E7");var subQ2=sQuery(id+"F1.wireOp",EDGE,"E6");var subQ3=sQuery(id+"F1.wireOp",EDGE,"E5");var subQ4=sQuery(id+"F1.wireOp",EDGE,"E4");var subQ5=sQuery(id+"F1.wireOp",EDGE,"E0");var subQ6=sQuery(id+"F1.wireOp",EDGE,"E14");var subQ7=sQuery(id+"F1.wireOp",EDGE,"E15.trimOffspring");var subQ8=sQuery(id+"F1.wireOp",EDGE,"E12");var subQ9=sQuery(id+"F1.wireOp",EDGE,"E11.trimOffspring");var subQ10=sQuery(id+"F1.wireOp",EDGE,"E1");var subQ11=sQuery(id+"F1.wireOp",EDGE,"E16.trimOffspring");var subQ12=sQuery(id+"F1.wireOp",EDGE,"E13");var subQ13=sQuery(id+"F1.wireOp",EDGE,"E10.trimOffspring");var subQ14=sQuery(id+"F1.wireOp",EDGE,"E2");Q0=makeQuery(id+"F6.boolean.opBoolean","SPLIT",FACE,{"disambiguationData":[TD([makeQuery(id+"F2.opExtrude","SWEPT_FACE",FACE,{"disambiguationData":[OSD([subQ5])]}),makeQuery(id+"F2.opExtrude","CAP_FACE",FACE,{"disambiguationData":[OSD([subQ5,subQ10,subQ9,subQ8,subQ7])],"isStart":false}),makeQuery(id+"F3.opExtrude","CAP_FACE",FACE,{"disambiguationData":[OSD([subQ10,subQ14,subQ13,subQ9,subQ8,subQ12,subQ7,subQ11])],"isStart":false}),makeQuery(id+"F3.opExtrude","SWEPT_FACE",FACE,{"disambiguationData":[OSD([subQ10,subQ9,subQ8,subQ7])]}),makeQuery(id+"F4.opExtrude","CAP_FACE",FACE,{"disambiguationData":[OSD([subQ14,subQ13,subQ12,subQ6,subQ11])],"isStart":false}),makeQuery(id+"F4.opExtrude","SWEPT_FACE",FACE,{"disambiguationData":[OSD([subQ14,subQ13,subQ12,subQ11])]}),makeQuery(id+"F5.opExtrude","CAP_FACE",FACE,{"disambiguationData":[OSD([sQuery(id+"F1.wireOp",EDGE,"E3"),subQ6])],"isStart":false}),makeQuery(id+"F5.opExtrude","SWEPT_FACE",FACE,{"disambiguationData":[OSD([subQ6])]}),makeQuery(id+"F6.opExtrude","SWEPT_FACE",FACE,{"disambiguationData":[OSD([subQ5]),TDD([makeQuery(id+"F1.imprint","IMPRINT",EDGE,{"disambiguationData":[TD([[makeQuery(id+"F1.imprint","INTERSECT",VERTEX,{"derivedFrom":[subQ5,subQ2]}),1.0]])],"derivedFrom":subQ5})])]}),makeQuery(id+"F6.opExtrude","CAP_FACE",FACE,{"disambiguationData":[OSD([subQ5,subQ4,subQ3,subQ2,subQ1,subQ0,sQuery(id+"F1.wireOp",EDGE,"E18")])],"isStart":false}),makeQuery(id+"F6.opExtrude","SWEPT_FACE",FACE,{"disambiguationData":[OSD([subQ5]),TDD([makeQuery(id+"F1.imprint","IMPRINT",EDGE,{"disambiguationData":[TD([[makeQuery(id+"F1.imprint","INTERSECT",VERTEX,{"derivedFrom":[subQ5,subQ4]}),-1.0]])],"derivedFrom":subQ5})])]})]),OD(1.0)],"derivedFrom":makeQuery(id+"F6.opExtrude","SWEPT_FACE",FACE,{"disambiguationData":[OSD([subQ4,subQ2,subQ0])]})});}
            var sketch = newSketch(context, id + "F14", { "sketchPlane" : qUnion([Q0])});
            skLineSegment(sketch, "E57", {"start": v(-47.74, 12.7) * mm, "end": v(-7.65, 50.8) * mm});
            skLineSegment(sketch, "E58", {"start": v(-7.65, 50.8) * mm, "end": v(-7.65, 52.59) * mm});
            skLineSegment(sketch, "E59", {"start": v(-7.65, 52.59) * mm, "end": v(-58.24, 53.24) * mm});
            skLineSegment(sketch, "E60", {"start": v(-58.24, 53.24) * mm, "end": v(-54.04, 12.7) * mm});
            skLineSegment(sketch, "E61", {"start": v(-54.04, 12.7) * mm, "end": v(-47.74, 12.7) * mm});
            skPoint(sketch, "E62", {"position": v(-47, 12.7) * mm});
            skSolve(sketch);
        }
        {
            var Q0;
            Q0=qSketchRegion(id+"F14",true);
            extrude(context, id + "F15", {"entities" : qUnion([Q0]), "operationType" : NewBodyOperationType.REMOVE, "oppositeDirection" : true, "depth" : 15.24 * mm});
        }
        {
            var Q0;
            Q0=qCreatedBy(id+"F0.planeOp",FACE);
            var sketch = newSketch(context, id + "F16", { "sketchPlane" : qUnion([Q0])});
            skLineSegment(sketch, "E63.bottom", {"start": v(3.95, -2.54) * mm, "end": v(45.36, -2.54) * mm});
            skLineSegment(sketch, "E63.top", {"start": v(3.95, 2.54) * mm, "end": v(45.36, 2.54) * mm});
            skLineSegment(sketch, "E63.left", {"start": v(3.95, -2.54) * mm, "end": v(3.95, 2.54) * mm});
            skLineSegment(sketch, "E63.right", {"start": v(45.36, -2.54) * mm, "end": v(45.36, 2.54) * mm});
            skLineSegment(sketch, "E64.bottom", {"start": v(-4.1, -2.54) * mm, "end": v(-45.5, -2.54) * mm});
            skLineSegment(sketch, "E64.top", {"start": v(-4.1, 2.54) * mm, "end": v(-45.5, 2.54) * mm});
            skLineSegment(sketch, "E64.left", {"start": v(-4.1, -2.54) * mm, "end": v(-4.1, 2.54) * mm});
            skLineSegment(sketch, "E64.right", {"start": v(-45.5, -2.54) * mm, "end": v(-45.5, 2.54) * mm});
            skLineSegment(sketch, "E65.bottom", {"start": v(-2.54, 3.8) * mm, "end": v(2.54, 3.8) * mm});
            skLineSegment(sketch, "E65.top", {"start": v(-2.54, 45.2) * mm, "end": v(2.54, 45.2) * mm});
            skLineSegment(sketch, "E65.left", {"start": v(-2.54, 3.8) * mm, "end": v(-2.54, 45.2) * mm});
            skLineSegment(sketch, "E65.right", {"start": v(2.54, 3.8) * mm, "end": v(2.54, 45.2) * mm});
            skLineSegment(sketch, "E66.bottom", {"start": v(-2.54, -3.85) * mm, "end": v(2.54, -3.85) * mm});
            skLineSegment(sketch, "E66.top", {"start": v(-2.54, -45.25) * mm, "end": v(2.54, -45.25) * mm});
            skLineSegment(sketch, "E66.left", {"start": v(-2.54, -3.85) * mm, "end": v(-2.54, -45.25) * mm});
            skLineSegment(sketch, "E66.right", {"start": v(2.54, -3.85) * mm, "end": v(2.54, -45.25) * mm});
            skSolve(sketch);
        }
        {
            var Q0;
            Q0=qSketchRegion(id+"F16",true);
            extrude(context, id + "F17", {"entities" : qUnion([Q0]), "operationType" : NewBodyOperationType.REMOVE, "oppositeDirection" : true, "depth" : 44.45 * mm});
        }
        {
            var Q0;
            {var subQ0=sQuery(id+"F1.wireOp",EDGE,"E22");var subQ4=sQuery(id+"F1.wireOp",EDGE,"E3");var subQ5=makeQuery(id+"F1.imprint","INTERSECT",VERTEX,{"derivedFrom":[subQ4,subQ0]});Q0=makeQuery(id+"F1.imprint","IMPRINT",FACE,{"disambiguationData":[TD([[makeQuery(id+"F1.imprint","IMPRINT",EDGE,{"disambiguationData":[TD([[subQ5,-1.0]])],"derivedFrom":subQ4}),1.0]])]});}
            var Q1;
            {var subQ3=sQuery(id+"F1.wireOp",EDGE,"E3");var subQ5=sQuery(id+"F1.wireOp",EDGE,"E22");var subQ6=makeQuery(id+"F1.imprint","INTERSECT",VERTEX,{"derivedFrom":[subQ3,subQ5]});Q1=makeQuery(id+"F1.imprint","IMPRINT",FACE,{"disambiguationData":[TD([[makeQuery(id+"F1.imprint","IMPRINT",EDGE,{"disambiguationData":[TD([[subQ6,-1.0]])],"derivedFrom":subQ3}),-1.0]])]});}
            var Q2;
            {var subQ0=sQuery(id+"F1.wireOp",EDGE,"E22");var subQ1=sQuery(id+"F1.wireOp",EDGE,"E10.trimOffspring");var subQ2=makeQuery(id+"F1.imprint","INTERSECT",VERTEX,{"derivedFrom":[subQ1,subQ0]});Q2=makeQuery(id+"F1.imprint","IMPRINT",FACE,{"disambiguationData":[TD([[makeQuery(id+"F1.imprint","IMPRINT",EDGE,{"disambiguationData":[TD([[subQ2,-1.0]])],"derivedFrom":subQ1}),1.0]])]});}
            var Q3;
            {var subQ0=sQuery(id+"F1.wireOp",EDGE,"E22");var subQ1=sQuery(id+"F1.wireOp",EDGE,"E10.trimOffspring");var subQ2=makeQuery(id+"F1.imprint","INTERSECT",VERTEX,{"derivedFrom":[subQ1,subQ0]});Q3=makeQuery(id+"F1.imprint","IMPRINT",FACE,{"disambiguationData":[TD([[makeQuery(id+"F1.imprint","IMPRINT",EDGE,{"disambiguationData":[TD([[subQ2,-1.0]])],"derivedFrom":subQ1}),-1.0]])]});}
            var Q4;
            {var subQ0=sQuery(id+"F1.wireOp",EDGE,"E22");var subQ1=sQuery(id+"F1.wireOp",EDGE,"E0");var subQ2=makeQuery(id+"F1.imprint","INTERSECT",VERTEX,{"derivedFrom":[subQ1,subQ0]});Q4=makeQuery(id+"F1.imprint","IMPRINT",FACE,{"disambiguationData":[TD([[makeQuery(id+"F1.imprint","IMPRINT",EDGE,{"disambiguationData":[TD([[subQ2,-1.0]])],"derivedFrom":subQ1}),1.0]])]});}
            var Q5;
            {var subQ0=sQuery(id+"F1.wireOp",EDGE,"E17");var subQ3=sQuery(id+"F1.wireOp",EDGE,"E27");var subQ5=makeQuery(id+"F1.imprint","INTERSECT",VERTEX,{"derivedFrom":[subQ0,subQ3]});Q5=makeQuery(id+"F1.imprint","IMPRINT",FACE,{"disambiguationData":[TD([[makeQuery(id+"F1.imprint","IMPRINT",EDGE,{"disambiguationData":[TD([[subQ5,-1.0]])],"derivedFrom":subQ3}),1.0]])]});}
            var Q6;
            {var subQ0=sQuery(id+"F1.wireOp",EDGE,"E14");var subQ1=sQuery(id+"F1.wireOp",EDGE,"E4");var subQ2=makeQuery(id+"F1.imprint","INTERSECT",VERTEX,{"derivedFrom":[subQ1,subQ0]});Q6=makeQuery(id+"F1.imprint","IMPRINT",FACE,{"disambiguationData":[TD([[makeQuery(id+"F1.imprint","IMPRINT",EDGE,{"disambiguationData":[TD([[subQ2,1.0]])],"derivedFrom":subQ0}),1.0]])]});}
            var Q7;
            {var subQ1=sQuery(id+"F1.wireOp",EDGE,"E4");var subQ7=sQuery(id+"F1.wireOp",EDGE,"E31");var subQ9=makeQuery(id+"F1.imprint","INTERSECT",VERTEX,{"derivedFrom":[subQ1,subQ7]});Q7=makeQuery(id+"F1.imprint","IMPRINT",FACE,{"disambiguationData":[TD([[makeQuery(id+"F1.imprint","IMPRINT",EDGE,{"disambiguationData":[TD([[subQ9,1.0]])],"derivedFrom":subQ1}),-1.0]])]});}
            var Q8;
            {var subQ0=sQuery(id+"F1.wireOp",EDGE,"E28");var subQ1=sQuery(id+"F1.wireOp",EDGE,"E10.trimOffspring");var subQ2=makeQuery(id+"F1.imprint","INTERSECT",VERTEX,{"derivedFrom":[subQ1,subQ0]});Q8=makeQuery(id+"F1.imprint","IMPRINT",FACE,{"disambiguationData":[TD([[makeQuery(id+"F1.imprint","IMPRINT",EDGE,{"disambiguationData":[TD([[subQ2,-1.0]])],"derivedFrom":subQ1}),-1.0]])]});}
            var Q9;
            {var subQ0=sQuery(id+"F1.wireOp",EDGE,"E28");var subQ1=sQuery(id+"F1.wireOp",EDGE,"E0");var subQ2=makeQuery(id+"F1.imprint","INTERSECT",VERTEX,{"derivedFrom":[subQ1,subQ0]});Q9=makeQuery(id+"F1.imprint","IMPRINT",FACE,{"disambiguationData":[TD([[makeQuery(id+"F1.imprint","IMPRINT",EDGE,{"disambiguationData":[TD([[subQ2,-1.0]])],"derivedFrom":subQ1}),1.0]])]});}
            var Q10;
            {var subQ0=sQuery(id+"F1.wireOp",EDGE,"E32");var subQ1=sQuery(id+"F1.wireOp",EDGE,"E0");var subQ2=makeQuery(id+"F1.imprint","INTERSECT",VERTEX,{"derivedFrom":[subQ1,subQ0]});Q10=makeQuery(id+"F1.imprint","IMPRINT",FACE,{"disambiguationData":[TD([[makeQuery(id+"F1.imprint","IMPRINT",EDGE,{"disambiguationData":[TD([[subQ2,1.0]])],"derivedFrom":subQ1}),1.0]])]});}
            var Q11;
            {var subQ0=sQuery(id+"F1.wireOp",EDGE,"E19");var subQ1=sQuery(id+"F1.wireOp",EDGE,"E0");var subQ2=makeQuery(id+"F1.imprint","INTERSECT",VERTEX,{"derivedFrom":[subQ1,subQ0]});Q11=makeQuery(id+"F1.imprint","IMPRINT",FACE,{"disambiguationData":[TD([[makeQuery(id+"F1.imprint","IMPRINT",EDGE,{"disambiguationData":[TD([[subQ2,1.0]])],"derivedFrom":subQ1}),1.0]])]});}
            var Q12;
            {var subQ0=sQuery(id+"F1.wireOp",EDGE,"E33");var subQ1=sQuery(id+"F1.wireOp",EDGE,"E10.trimOffspring");var subQ2=makeQuery(id+"F1.imprint","INTERSECT",VERTEX,{"derivedFrom":[subQ1,subQ0]});Q12=makeQuery(id+"F1.imprint","IMPRINT",FACE,{"disambiguationData":[TD([[makeQuery(id+"F1.imprint","IMPRINT",EDGE,{"disambiguationData":[TD([[subQ2,-1.0]])],"derivedFrom":subQ1}),-1.0]])]});}
            var Q13;
            {var subQ0=sQuery(id+"F1.wireOp",EDGE,"E32");var subQ1=sQuery(id+"F1.wireOp",EDGE,"E10.trimOffspring");var subQ2=makeQuery(id+"F1.imprint","INTERSECT",VERTEX,{"derivedFrom":[subQ1,subQ0]});Q13=makeQuery(id+"F1.imprint","IMPRINT",FACE,{"disambiguationData":[TD([[makeQuery(id+"F1.imprint","IMPRINT",EDGE,{"disambiguationData":[TD([[subQ2,-1.0]])],"derivedFrom":subQ1}),-1.0]])]});}
            var Q14;
            {var subQ5=sQuery(id+"F1.wireOp",EDGE,"E6");var subQ7=sQuery(id+"F1.wireOp",EDGE,"E33");var subQ9=makeQuery(id+"F1.imprint","INTERSECT",VERTEX,{"derivedFrom":[subQ5,subQ7]});Q14=makeQuery(id+"F1.imprint","IMPRINT",FACE,{"disambiguationData":[TD([[makeQuery(id+"F1.imprint","IMPRINT",EDGE,{"disambiguationData":[TD([[subQ9,1.0]])],"derivedFrom":subQ5}),1.0]])]});}
            var Q15;
            {var subQ0=sQuery(id+"F1.wireOp",EDGE,"E32");var subQ1=sQuery(id+"F1.wireOp",EDGE,"E10.trimOffspring");var subQ2=makeQuery(id+"F1.imprint","INTERSECT",VERTEX,{"derivedFrom":[subQ1,subQ0]});Q15=makeQuery(id+"F1.imprint","IMPRINT",FACE,{"disambiguationData":[TD([[makeQuery(id+"F1.imprint","IMPRINT",EDGE,{"disambiguationData":[TD([[subQ2,-1.0]])],"derivedFrom":subQ1}),1.0]])]});}
            var Q16;
            {var subQ0=sQuery(id+"F1.wireOp",EDGE,"E6");var subQ5=sQuery(id+"F1.wireOp",EDGE,"E14");var subQ6=makeQuery(id+"F1.imprint","INTERSECT",VERTEX,{"derivedFrom":[subQ0,subQ5]});Q16=makeQuery(id+"F1.imprint","IMPRINT",FACE,{"disambiguationData":[TD([[makeQuery(id+"F1.imprint","IMPRINT",EDGE,{"disambiguationData":[TD([[subQ6,-1.0]])],"derivedFrom":subQ5}),1.0]])]});}
            var Q17;
            {var subQ0=sQuery(id+"F1.wireOp",EDGE,"E32");var subQ1=sQuery(id+"F1.wireOp",EDGE,"E3");var subQ2=makeQuery(id+"F1.imprint","INTERSECT",VERTEX,{"derivedFrom":[subQ1,subQ0]});Q17=makeQuery(id+"F1.imprint","IMPRINT",FACE,{"disambiguationData":[TD([[makeQuery(id+"F1.imprint","IMPRINT",EDGE,{"disambiguationData":[TD([[subQ2,-1.0]])],"derivedFrom":subQ1}),-1.0]])]});}
            var Q18;
            {var subQ5=sQuery(id+"F1.wireOp",EDGE,"E32");var subQ7=sQuery(id+"F1.wireOp",EDGE,"E3");var subQ8=makeQuery(id+"F1.imprint","INTERSECT",VERTEX,{"derivedFrom":[subQ7,subQ5]});Q18=makeQuery(id+"F1.imprint","IMPRINT",FACE,{"disambiguationData":[TD([[makeQuery(id+"F1.imprint","IMPRINT",EDGE,{"disambiguationData":[TD([[subQ8,-1.0]])],"derivedFrom":subQ7}),1.0]])]});}
            var Q19;
            {var subQ0=sQuery(id+"F1.wireOp",EDGE,"E17");var subQ3=sQuery(id+"F1.wireOp",EDGE,"E32");var subQ5=makeQuery(id+"F1.imprint","INTERSECT",VERTEX,{"derivedFrom":[subQ0,subQ3]});Q19=makeQuery(id+"F1.imprint","IMPRINT",FACE,{"disambiguationData":[TD([[makeQuery(id+"F1.imprint","IMPRINT",EDGE,{"disambiguationData":[TD([[subQ5,-1.0]])],"derivedFrom":subQ3}),-1.0]])]});}
            var Q20;
            {var subQ0=sQuery(id+"F1.wireOp",EDGE,"E18");var subQ3=sQuery(id+"F1.wireOp",EDGE,"E36");var subQ5=makeQuery(id+"F1.imprint","INTERSECT",VERTEX,{"derivedFrom":[subQ0,subQ3]});Q20=makeQuery(id+"F1.imprint","IMPRINT",FACE,{"disambiguationData":[TD([[makeQuery(id+"F1.imprint","IMPRINT",EDGE,{"disambiguationData":[TD([[subQ5,-1.0]])],"derivedFrom":subQ3}),-1.0]])]});}
            var Q21;
            {var subQ0=sQuery(id+"F1.wireOp",EDGE,"E5");var subQ5=sQuery(id+"F1.wireOp",EDGE,"E14");var subQ6=makeQuery(id+"F1.imprint","INTERSECT",VERTEX,{"derivedFrom":[subQ0,subQ5]});Q21=makeQuery(id+"F1.imprint","IMPRINT",FACE,{"disambiguationData":[TD([[makeQuery(id+"F1.imprint","IMPRINT",EDGE,{"disambiguationData":[TD([[subQ6,-1.0]])],"derivedFrom":subQ5}),1.0]])]});}
            var Q22;
            {var subQ0=sQuery(id+"F1.wireOp",EDGE,"E37");var subQ1=sQuery(id+"F1.wireOp",EDGE,"E1");var subQ2=makeQuery(id+"F1.imprint","INTERSECT",VERTEX,{"derivedFrom":[subQ1,subQ0]});Q22=makeQuery(id+"F1.imprint","IMPRINT",FACE,{"disambiguationData":[TD([[makeQuery(id+"F1.imprint","IMPRINT",EDGE,{"disambiguationData":[TD([[subQ2,-1.0]])],"derivedFrom":subQ1}),1.0]])]});}
            var Q23;
            {var subQ1=sQuery(id+"F1.wireOp",EDGE,"E2");var subQ7=sQuery(id+"F1.wireOp",EDGE,"E37");var subQ9=makeQuery(id+"F1.imprint","INTERSECT",VERTEX,{"derivedFrom":[subQ1,subQ7]});Q23=makeQuery(id+"F1.imprint","IMPRINT",FACE,{"disambiguationData":[TD([[makeQuery(id+"F1.imprint","IMPRINT",EDGE,{"disambiguationData":[TD([[subQ9,-1.0]])],"derivedFrom":subQ1}),1.0]])]});}
            var Q24;
            {var subQ0=sQuery(id+"F1.wireOp",EDGE,"E36");var subQ1=sQuery(id+"F1.wireOp",EDGE,"E0");var subQ2=makeQuery(id+"F1.imprint","INTERSECT",VERTEX,{"derivedFrom":[subQ1,subQ0]});Q24=makeQuery(id+"F1.imprint","IMPRINT",FACE,{"disambiguationData":[TD([[makeQuery(id+"F1.imprint","IMPRINT",EDGE,{"disambiguationData":[TD([[subQ2,1.0]])],"derivedFrom":subQ1}),1.0]])]});}
            var Q25;
            {var subQ5=sQuery(id+"F1.wireOp",EDGE,"E36");var subQ7=sQuery(id+"F1.wireOp",EDGE,"E3");var subQ9=makeQuery(id+"F1.imprint","INTERSECT",VERTEX,{"derivedFrom":[subQ7,subQ5]});Q25=makeQuery(id+"F1.imprint","IMPRINT",FACE,{"disambiguationData":[TD([[makeQuery(id+"F1.imprint","IMPRINT",EDGE,{"disambiguationData":[TD([[subQ9,-1.0]])],"derivedFrom":subQ7}),1.0]])]});}
            var Q26;
            {var subQ0=sQuery(id+"F1.wireOp",EDGE,"E36");var subQ1=sQuery(id+"F1.wireOp",EDGE,"E3");var subQ2=makeQuery(id+"F1.imprint","INTERSECT",VERTEX,{"derivedFrom":[subQ1,subQ0]});Q26=makeQuery(id+"F1.imprint","IMPRINT",FACE,{"disambiguationData":[TD([[makeQuery(id+"F1.imprint","IMPRINT",EDGE,{"disambiguationData":[TD([[subQ2,-1.0]])],"derivedFrom":subQ1}),-1.0]])]});}
            var Q27;
            {var subQ0=sQuery(id+"F1.wireOp",EDGE,"E36");var subQ1=sQuery(id+"F1.wireOp",EDGE,"E2");var subQ2=makeQuery(id+"F1.imprint","INTERSECT",VERTEX,{"derivedFrom":[subQ1,subQ0]});Q27=makeQuery(id+"F1.imprint","IMPRINT",FACE,{"disambiguationData":[TD([[makeQuery(id+"F1.imprint","IMPRINT",EDGE,{"disambiguationData":[TD([[subQ2,-1.0]])],"derivedFrom":subQ1}),1.0]])]});}
            var Q28;
            {var subQ0=sQuery(id+"F1.wireOp",EDGE,"E36");var subQ1=sQuery(id+"F1.wireOp",EDGE,"E1");var subQ2=makeQuery(id+"F1.imprint","INTERSECT",VERTEX,{"derivedFrom":[subQ1,subQ0]});Q28=makeQuery(id+"F1.imprint","IMPRINT",FACE,{"disambiguationData":[TD([[makeQuery(id+"F1.imprint","IMPRINT",EDGE,{"disambiguationData":[TD([[subQ2,-1.0]])],"derivedFrom":subQ1}),1.0]])]});}
            var Q29;
            {var subQ0=sQuery(id+"F1.wireOp",EDGE,"E21");var subQ1=sQuery(id+"F1.wireOp",EDGE,"E0");var subQ2=makeQuery(id+"F1.imprint","INTERSECT",VERTEX,{"derivedFrom":[subQ1,subQ0]});Q29=makeQuery(id+"F1.imprint","IMPRINT",FACE,{"disambiguationData":[TD([[makeQuery(id+"F1.imprint","IMPRINT",EDGE,{"disambiguationData":[TD([[subQ2,1.0]])],"derivedFrom":subQ1}),1.0]])]});}
            var Q30;
            {var subQ5=sQuery(id+"F1.wireOp",EDGE,"E35");var subQ7=sQuery(id+"F1.wireOp",EDGE,"E3");var subQ8=makeQuery(id+"F1.imprint","INTERSECT",VERTEX,{"derivedFrom":[subQ7,subQ5]});Q30=makeQuery(id+"F1.imprint","IMPRINT",FACE,{"disambiguationData":[TD([[makeQuery(id+"F1.imprint","IMPRINT",EDGE,{"disambiguationData":[TD([[subQ8,1.0]])],"derivedFrom":subQ7}),1.0]])]});}
            var Q31;
            {var subQ0=sQuery(id+"F1.wireOp",EDGE,"E35");var subQ1=sQuery(id+"F1.wireOp",EDGE,"E3");var subQ2=makeQuery(id+"F1.imprint","INTERSECT",VERTEX,{"derivedFrom":[subQ1,subQ0]});Q31=makeQuery(id+"F1.imprint","IMPRINT",FACE,{"disambiguationData":[TD([[makeQuery(id+"F1.imprint","IMPRINT",EDGE,{"disambiguationData":[TD([[subQ2,1.0]])],"derivedFrom":subQ1}),-1.0]])]});}
            var Q32;
            {var subQ0=sQuery(id+"F1.wireOp",EDGE,"E20");var subQ1=sQuery(id+"F1.wireOp",EDGE,"E2");var subQ2=makeQuery(id+"F1.imprint","INTERSECT",VERTEX,{"derivedFrom":[subQ1,subQ0]});Q32=makeQuery(id+"F1.imprint","IMPRINT",FACE,{"disambiguationData":[TD([[makeQuery(id+"F1.imprint","IMPRINT",EDGE,{"disambiguationData":[TD([[subQ2,-1.0]])],"derivedFrom":subQ1}),1.0]])]});}
            var Q33;
            {var subQ0=sQuery(id+"F1.wireOp",EDGE,"E20");var subQ1=sQuery(id+"F1.wireOp",EDGE,"E1");var subQ2=makeQuery(id+"F1.imprint","INTERSECT",VERTEX,{"derivedFrom":[subQ1,subQ0]});Q33=makeQuery(id+"F1.imprint","IMPRINT",FACE,{"disambiguationData":[TD([[makeQuery(id+"F1.imprint","IMPRINT",EDGE,{"disambiguationData":[TD([[subQ2,-1.0]])],"derivedFrom":subQ1}),1.0]])]});}
            var Q34;
            {var subQ0=sQuery(id+"F1.wireOp",EDGE,"E20");var subQ1=sQuery(id+"F1.wireOp",EDGE,"E0");var subQ2=makeQuery(id+"F1.imprint","INTERSECT",VERTEX,{"derivedFrom":[subQ1,subQ0]});Q34=makeQuery(id+"F1.imprint","IMPRINT",FACE,{"disambiguationData":[TD([[makeQuery(id+"F1.imprint","IMPRINT",EDGE,{"disambiguationData":[TD([[subQ2,-1.0]])],"derivedFrom":subQ1}),1.0]])]});}
            var Q35;
            {var subQ0=sQuery(id+"F1.wireOp",EDGE,"E34");var subQ1=sQuery(id+"F1.wireOp",EDGE,"E0");var subQ2=makeQuery(id+"F1.imprint","INTERSECT",VERTEX,{"derivedFrom":[subQ1,subQ0]});Q35=makeQuery(id+"F1.imprint","IMPRINT",FACE,{"disambiguationData":[TD([[makeQuery(id+"F1.imprint","IMPRINT",EDGE,{"disambiguationData":[TD([[subQ2,1.0]])],"derivedFrom":subQ1}),1.0]])]});}
            var Q36;
            {var subQ0=sQuery(id+"F1.wireOp",EDGE,"E35");var subQ1=sQuery(id+"F1.wireOp",EDGE,"E1");var subQ2=makeQuery(id+"F1.imprint","INTERSECT",VERTEX,{"derivedFrom":[subQ1,subQ0]});Q36=makeQuery(id+"F1.imprint","IMPRINT",FACE,{"disambiguationData":[TD([[makeQuery(id+"F1.imprint","IMPRINT",EDGE,{"disambiguationData":[TD([[subQ2,-1.0]])],"derivedFrom":subQ1}),1.0]])]});}
            var Q37;
            {var subQ3=sQuery(id+"F1.wireOp",EDGE,"E2");var subQ5=sQuery(id+"F1.wireOp",EDGE,"E35");var subQ6=makeQuery(id+"F1.imprint","INTERSECT",VERTEX,{"derivedFrom":[subQ3,subQ5]});Q37=makeQuery(id+"F1.imprint","IMPRINT",FACE,{"disambiguationData":[TD([[makeQuery(id+"F1.imprint","IMPRINT",EDGE,{"disambiguationData":[TD([[subQ6,-1.0]])],"derivedFrom":subQ3}),1.0]])]});}
            var Q38;
            {var subQ0=sQuery(id+"F1.wireOp",EDGE,"E7");var subQ5=sQuery(id+"F1.wireOp",EDGE,"E14");var subQ7=makeQuery(id+"F1.imprint","INTERSECT",VERTEX,{"derivedFrom":[subQ0,subQ5]});Q38=makeQuery(id+"F1.imprint","IMPRINT",FACE,{"disambiguationData":[TD([[makeQuery(id+"F1.imprint","IMPRINT",EDGE,{"disambiguationData":[TD([[subQ7,1.0]])],"derivedFrom":subQ5}),1.0]])]});}
            var Q39;
            {var subQ0=sQuery(id+"F1.wireOp",EDGE,"E18");var subQ3=sQuery(id+"F1.wireOp",EDGE,"E35");var subQ5=makeQuery(id+"F1.imprint","INTERSECT",VERTEX,{"derivedFrom":[subQ0,subQ3]});Q39=makeQuery(id+"F1.imprint","IMPRINT",FACE,{"disambiguationData":[TD([[makeQuery(id+"F1.imprint","IMPRINT",EDGE,{"disambiguationData":[TD([[subQ5,-1.0]])],"derivedFrom":subQ3}),1.0]])]});}
            var Q40;
            {var subQ0=sQuery(id+"F1.wireOp",EDGE,"E35");var subQ1=sQuery(id+"F1.wireOp",EDGE,"E2");var subQ2=makeQuery(id+"F1.imprint","INTERSECT",VERTEX,{"derivedFrom":[subQ1,subQ0]});Q40=makeQuery(id+"F1.imprint","IMPRINT",FACE,{"disambiguationData":[TD([[makeQuery(id+"F1.imprint","IMPRINT",EDGE,{"disambiguationData":[TD([[subQ2,-1.0]])],"derivedFrom":subQ1}),-1.0]])]});}
            var Q41;
            {var subQ4=sQuery(id+"F1.wireOp",EDGE,"E20");var subQ5=sQuery(id+"F1.wireOp",EDGE,"E2");var subQ6=makeQuery(id+"F1.imprint","INTERSECT",VERTEX,{"derivedFrom":[subQ5,subQ4]});Q41=makeQuery(id+"F1.imprint","IMPRINT",FACE,{"disambiguationData":[TD([[makeQuery(id+"F1.imprint","IMPRINT",EDGE,{"disambiguationData":[TD([[subQ6,-1.0]])],"derivedFrom":subQ5}),-1.0]])]});}
            var Q42;
            {var subQ0=sQuery(id+"F1.wireOp",EDGE,"E36");var subQ4=sQuery(id+"F1.wireOp",EDGE,"E2");var subQ5=makeQuery(id+"F1.imprint","INTERSECT",VERTEX,{"derivedFrom":[subQ4,subQ0]});Q42=makeQuery(id+"F1.imprint","IMPRINT",FACE,{"disambiguationData":[TD([[makeQuery(id+"F1.imprint","IMPRINT",EDGE,{"disambiguationData":[TD([[subQ5,-1.0]])],"derivedFrom":subQ4}),-1.0]])]});}
            extrude(context, id + "F18", {"entities" : qUnion([Q0, Q1, Q2, Q3, Q4, Q5, Q6, Q7, Q8, Q9, Q10, Q11, Q12, Q13, Q14, Q15, Q16, Q17, Q18, Q19, Q20, Q21, Q22, Q23, Q24, Q25, Q26, Q27, Q28, Q29, Q30, Q31, Q32, Q33, Q34, Q35, Q36, Q37, Q38, Q39, Q40, Q41, Q42]), "operationType" : NewBodyOperationType.ADD, "depth" : 50.8 * mm});
        }
        {
            var Q0;
            Q0=qCreatedBy(id+"F0.planeOp",FACE);
            var sketch = newSketch(context, id + "F19", { "sketchPlane" : qUnion([Q0])});
            skLineSegment(sketch, "E67", {"start": v(-10.16, -10.16) * mm, "end": v(-10.16, -12.7) * mm});
            skLineSegment(sketch, "E68", {"start": v(-10.16, -10.16) * mm, "end": v(-38.1, -10.16) * mm});
            skLineSegment(sketch, "E69", {"start": v(-38.1, -10.16) * mm, "end": v(-38.1, -12.7) * mm});
            skLineSegment(sketch, "E70", {"start": v(-38.1, -12.7) * mm, "end": v(-10.16, -12.7) * mm});
            skLineSegment(sketch, "E71", {"start": v(-10.16, -15.24) * mm, "end": v(-10.16, -17.78) * mm});
            skLineSegment(sketch, "E72", {"start": v(-10.16, -15.24) * mm, "end": v(-38.1, -15.24) * mm});
            skLineSegment(sketch, "E73", {"start": v(-38.1, -15.24) * mm, "end": v(-38.1, -17.78) * mm});
            skLineSegment(sketch, "E74", {"start": v(-38.1, -17.78) * mm, "end": v(-10.16, -17.78) * mm});
            skLineSegment(sketch, "E75", {"start": v(-10.16, 10.16) * mm, "end": v(-38.1, 10.16) * mm});
            skLineSegment(sketch, "E76", {"start": v(-38.1, 10.16) * mm, "end": v(-38.1, 12.7) * mm});
            skLineSegment(sketch, "E77", {"start": v(-38.1, 12.7) * mm, "end": v(-10.16, 12.7) * mm});
            skLineSegment(sketch, "E78", {"start": v(-10.16, 12.7) * mm, "end": v(-10.16, 10.16) * mm});
            skLineSegment(sketch, "E79", {"start": v(-10.16, 15.24) * mm, "end": v(-10.16, 17.78) * mm});
            skLineSegment(sketch, "E80", {"start": v(-10.16, 17.78) * mm, "end": v(-38.1, 17.78) * mm});
            skLineSegment(sketch, "E81", {"start": v(-38.1, 17.78) * mm, "end": v(-38.1, 15.24) * mm});
            skLineSegment(sketch, "E82", {"start": v(-38.1, 15.24) * mm, "end": v(-10.16, 15.24) * mm});
            skLineSegment(sketch, "E83", {"start": v(10.16, 17.78) * mm, "end": v(38.1, 17.78) * mm});
            skLineSegment(sketch, "E84", {"start": v(38.1, 17.78) * mm, "end": v(38.1, 15.24) * mm});
            skLineSegment(sketch, "E85", {"start": v(38.1, 15.24) * mm, "end": v(10.16, 15.24) * mm});
            skLineSegment(sketch, "E86", {"start": v(10.16, 15.24) * mm, "end": v(10.16, 17.78) * mm});
            skLineSegment(sketch, "E87", {"start": v(10.16, 12.7) * mm, "end": v(38.1, 12.7) * mm});
            skLineSegment(sketch, "E88", {"start": v(38.1, 12.7) * mm, "end": v(38.1, 10.16) * mm});
            skLineSegment(sketch, "E89", {"start": v(38.1, 10.16) * mm, "end": v(10.16, 10.16) * mm});
            skLineSegment(sketch, "E90", {"start": v(10.16, 10.16) * mm, "end": v(10.16, 12.7) * mm});
            skLineSegment(sketch, "E91", {"start": v(10.16, -10.16) * mm, "end": v(38.1, -10.16) * mm});
            skLineSegment(sketch, "E92", {"start": v(38.1, -10.16) * mm, "end": v(38.1, -12.7) * mm});
            skLineSegment(sketch, "E93", {"start": v(38.1, -12.7) * mm, "end": v(10.16, -12.7) * mm});
            skLineSegment(sketch, "E94", {"start": v(10.16, -12.7) * mm, "end": v(10.16, -10.16) * mm});
            skLineSegment(sketch, "E95", {"start": v(10.16, -15.24) * mm, "end": v(38.1, -15.24) * mm});
            skLineSegment(sketch, "E96", {"start": v(38.1, -15.24) * mm, "end": v(38.1, -17.78) * mm});
            skLineSegment(sketch, "E97", {"start": v(38.1, -17.78) * mm, "end": v(10.16, -17.78) * mm});
            skLineSegment(sketch, "E98", {"start": v(10.16, -17.78) * mm, "end": v(10.16, -15.24) * mm});
            skLineSegment(sketch, "E99", {"start": v(-10.16, 20.32) * mm, "end": v(-38.1, 20.32) * mm});
            skLineSegment(sketch, "E100", {"start": v(-10.16, 20.32) * mm, "end": v(-10.16, 22.86) * mm});
            skLineSegment(sketch, "E101", {"start": v(-10.16, 22.86) * mm, "end": v(-38.1, 22.86) * mm});
            skLineSegment(sketch, "E102", {"start": v(-38.1, 22.86) * mm, "end": v(-38.1, 20.32) * mm});
            skLineSegment(sketch, "E103", {"start": v(-10.16, 25.4) * mm, "end": v(-38.1, 25.4) * mm});
            skLineSegment(sketch, "E104", {"start": v(-38.1, 25.4) * mm, "end": v(-38.1, 27.94) * mm});
            skLineSegment(sketch, "E105", {"start": v(-38.1, 27.94) * mm, "end": v(-10.16, 27.94) * mm});
            skLineSegment(sketch, "E106", {"start": v(-10.16, 27.94) * mm, "end": v(-10.16, 25.4) * mm});
            skLineSegment(sketch, "E107.bottom", {"start": v(-10.16, -20.32) * mm, "end": v(-38.1, -20.32) * mm});
            skLineSegment(sketch, "E107.top", {"start": v(-10.16, -22.86) * mm, "end": v(-38.1, -22.86) * mm});
            skLineSegment(sketch, "E107.left", {"start": v(-10.16, -20.32) * mm, "end": v(-10.16, -22.86) * mm});
            skLineSegment(sketch, "E107.right", {"start": v(-38.1, -20.32) * mm, "end": v(-38.1, -22.86) * mm});
            skLineSegment(sketch, "E108.bottom", {"start": v(-10.16, -25.4) * mm, "end": v(-38.1, -25.4) * mm});
            skLineSegment(sketch, "E108.top", {"start": v(-10.16, -27.94) * mm, "end": v(-38.1, -27.94) * mm});
            skLineSegment(sketch, "E108.left", {"start": v(-10.16, -25.4) * mm, "end": v(-10.16, -27.94) * mm});
            skLineSegment(sketch, "E108.right", {"start": v(-38.1, -25.4) * mm, "end": v(-38.1, -27.94) * mm});
            skLineSegment(sketch, "E109.bottom", {"start": v(10.16, -20.32) * mm, "end": v(38.1, -20.32) * mm});
            skLineSegment(sketch, "E109.top", {"start": v(10.16, -22.86) * mm, "end": v(38.1, -22.86) * mm});
            skLineSegment(sketch, "E109.left", {"start": v(10.16, -20.32) * mm, "end": v(10.16, -22.86) * mm});
            skLineSegment(sketch, "E109.right", {"start": v(38.1, -20.32) * mm, "end": v(38.1, -22.86) * mm});
            skLineSegment(sketch, "E110.bottom", {"start": v(10.16, -25.4) * mm, "end": v(38.1, -25.4) * mm});
            skLineSegment(sketch, "E110.top", {"start": v(10.16, -27.94) * mm, "end": v(38.1, -27.94) * mm});
            skLineSegment(sketch, "E110.left", {"start": v(10.16, -25.4) * mm, "end": v(10.16, -27.94) * mm});
            skLineSegment(sketch, "E110.right", {"start": v(38.1, -25.4) * mm, "end": v(38.1, -27.94) * mm});
            skLineSegment(sketch, "E111.bottom", {"start": v(10.16, 20.32) * mm, "end": v(38.1, 20.32) * mm});
            skLineSegment(sketch, "E111.top", {"start": v(10.16, 22.86) * mm, "end": v(38.1, 22.86) * mm});
            skLineSegment(sketch, "E111.left", {"start": v(10.16, 20.32) * mm, "end": v(10.16, 22.86) * mm});
            skLineSegment(sketch, "E111.right", {"start": v(38.1, 20.32) * mm, "end": v(38.1, 22.86) * mm});
            skLineSegment(sketch, "E112.bottom", {"start": v(10.16, 25.4) * mm, "end": v(38.1, 25.4) * mm});
            skLineSegment(sketch, "E112.top", {"start": v(10.16, 27.94) * mm, "end": v(38.1, 27.94) * mm});
            skLineSegment(sketch, "E112.left", {"start": v(10.16, 25.4) * mm, "end": v(10.16, 27.94) * mm});
            skLineSegment(sketch, "E112.right", {"start": v(38.1, 25.4) * mm, "end": v(38.1, 27.94) * mm});
            skSolve(sketch);
        }
        {
            var Q0;
            Q0=makeQuery(id+"F18.opExtrude","SWEPT_FACE",FACE,{"disambiguationData":[OSD([sQuery(id+"F1.wireOp",EDGE,"E31")])]});
            var sketch = newSketch(context, id + "F20", { "sketchPlane" : qUnion([Q0])});
            skLineSegment(sketch, "E113", {"start": v(-7.62, 50.8) * mm, "end": v(-39.37, 12.7) * mm});
            skLineSegment(sketch, "E114", {"start": v(-39.37, 12.7) * mm, "end": v(-60.1, 12.7) * mm});
            skLineSegment(sketch, "E115", {"start": v(-60.1, 12.7) * mm, "end": v(-60.1, 65.61) * mm});
            skLineSegment(sketch, "E116", {"start": v(-60.1, 65.61) * mm, "end": v(-7.62, 65.61) * mm});
            skLineSegment(sketch, "E117", {"start": v(-7.62, 65.61) * mm, "end": v(-7.62, 50.8) * mm});
            skSolve(sketch);
        }
        {
            var Q0;
            Q0=qSketchRegion(id+"F20",true);
            extrude(context, id + "F21", {"entities" : qUnion([Q0]), "operationType" : NewBodyOperationType.REMOVE, "oppositeDirection" : true, "depth" : 24.49 * mm});
        }
        {
            var Q0;
            Q0=qSketchRegion(id+"F19",true);
            extrude(context, id + "F22", {"entities" : qUnion([Q0]), "operationType" : NewBodyOperationType.REMOVE, "oppositeDirection" : true, "depth" : 44.45 * mm});
        }
        {
            var Q0;
            Q0=makeQuery(id+"F18.opExtrude","SWEPT_FACE",FACE,{"disambiguationData":[OSD([sQuery(id+"F1.wireOp",EDGE,"E33")])]});
            var sketch = newSketch(context, id + "F23", { "sketchPlane" : qUnion([Q0])});
            skLineSegment(sketch, "E118", {"start": v(7.62, 50.8) * mm, "end": v(39.37, 12.7) * mm});
            skLineSegment(sketch, "E119", {"start": v(39.37, 12.7) * mm, "end": v(63.4, 12.7) * mm});
            skLineSegment(sketch, "E120", {"start": v(63.4, 12.7) * mm, "end": v(63.4, 58.95) * mm});
            skLineSegment(sketch, "E121", {"start": v(63.4, 58.95) * mm, "end": v(7.62, 58.95) * mm});
            skLineSegment(sketch, "E122", {"start": v(7.62, 58.95) * mm, "end": v(7.62, 50.8) * mm});
            skSolve(sketch);
        }
        {
            var Q0;
            Q0=qSketchRegion(id+"F23",true);
            extrude(context, id + "F24", {"entities" : qUnion([Q0]), "operationType" : NewBodyOperationType.REMOVE, "oppositeDirection" : true, "depth" : 24.49 * mm});
        }
        {
            var Q0;
            Q0=makeQuery(id+"F18.opExtrude","SWEPT_FACE",FACE,{"disambiguationData":[OSD([sQuery(id+"F1.wireOp",EDGE,"E34")])]});
            var sketch = newSketch(context, id + "F25", { "sketchPlane" : qUnion([Q0])});
            skLineSegment(sketch, "E123", {"start": v(-7.62, 50.8) * mm, "end": v(-39.37, 12.7) * mm});
            skLineSegment(sketch, "E124", {"start": v(-39.37, 12.7) * mm, "end": v(-64.42, 12.7) * mm});
            skLineSegment(sketch, "E125", {"start": v(-64.42, 12.7) * mm, "end": v(-64.42, 60.83) * mm});
            skLineSegment(sketch, "E126", {"start": v(-64.42, 60.83) * mm, "end": v(-7.62, 60.83) * mm});
            skLineSegment(sketch, "E127", {"start": v(-7.62, 60.83) * mm, "end": v(-7.62, 50.8) * mm});
            skSolve(sketch);
        }
        {
            var Q0;
            Q0=qSketchRegion(id+"F25",true);
            extrude(context, id + "F26", {"entities" : qUnion([Q0]), "operationType" : NewBodyOperationType.REMOVE, "oppositeDirection" : true, "depth" : 24.49 * mm});
        }
        {
            var Q0;
            Q0=makeQuery(id+"F18.opExtrude","SWEPT_FACE",FACE,{"disambiguationData":[OSD([sQuery(id+"F1.wireOp",EDGE,"E37")])]});
            var sketch = newSketch(context, id + "F27", { "sketchPlane" : qUnion([Q0])});
            skLineSegment(sketch, "E128", {"start": v(7.62, 50.8) * mm, "end": v(39.37, 12.7) * mm});
            skLineSegment(sketch, "E129", {"start": v(39.37, 12.7) * mm, "end": v(79.1, 12.7) * mm});
            skLineSegment(sketch, "E130", {"start": v(79.1, 12.7) * mm, "end": v(79.1, 63.6) * mm});
            skLineSegment(sketch, "E131", {"start": v(79.1, 63.6) * mm, "end": v(7.62, 58.32) * mm});
            skLineSegment(sketch, "E132", {"start": v(7.62, 58.32) * mm, "end": v(7.62, 50.8) * mm});
            skSolve(sketch);
        }
        {
            var Q0;
            Q0=qSketchRegion(id+"F27",true);
            extrude(context, id + "F28", {"entities" : qUnion([Q0]), "operationType" : NewBodyOperationType.REMOVE, "oppositeDirection" : true, "depth" : 24.49 * mm});
        }
        {
            var Q0;
            {var subQ5=sQuery(id+"F1.wireOp",EDGE,"E29.trimOffspring");Q0=makeQuery(id+"F1.imprint","IMPRINT",FACE,{"disambiguationData":[TD([[makeQuery(id+"F1.imprint","IMPRINT",EDGE,{"derivedFrom":subQ5}),1.0]])]});}
            var Q1;
            {var subQ0=sQuery(id+"F1.wireOp",EDGE,"E29.trimOffspring");Q1=makeQuery(id+"F1.imprint","IMPRINT",FACE,{"disambiguationData":[TD([[makeQuery(id+"F1.imprint","IMPRINT",EDGE,{"derivedFrom":subQ0}),-1.0]])]});}
            var Q2;
            {var subQ0=sQuery(id+"F1.wireOp",EDGE,"E5");var subQ3=sQuery(id+"F1.wireOp",EDGE,"E37");var subQ5=makeQuery(id+"F1.imprint","INTERSECT",VERTEX,{"derivedFrom":[subQ0,subQ3]});Q2=makeQuery(id+"F1.imprint","IMPRINT",FACE,{"disambiguationData":[TD([[makeQuery(id+"F1.imprint","IMPRINT",EDGE,{"disambiguationData":[TD([[subQ5,-1.0]])],"derivedFrom":subQ3}),-1.0]])]});}
            var Q3;
            {var subQ1=sQuery(id+"F1.wireOp",EDGE,"E1");var subQ3=sQuery(id+"F1.wireOp",EDGE,"E34");var subQ4=makeQuery(id+"F1.imprint","INTERSECT",VERTEX,{"derivedFrom":[subQ1,subQ3]});Q3=makeQuery(id+"F1.imprint","IMPRINT",FACE,{"disambiguationData":[TD([[makeQuery(id+"F1.imprint","IMPRINT",EDGE,{"disambiguationData":[TD([[subQ4,1.0]])],"derivedFrom":subQ3}),1.0]])]});}
            var Q4;
            {var subQ0=sQuery(id+"F1.wireOp",EDGE,"E7");var subQ3=sQuery(id+"F1.wireOp",EDGE,"E34");var subQ5=makeQuery(id+"F1.imprint","INTERSECT",VERTEX,{"derivedFrom":[subQ0,subQ3]});Q4=makeQuery(id+"F1.imprint","IMPRINT",FACE,{"disambiguationData":[TD([[makeQuery(id+"F1.imprint","IMPRINT",EDGE,{"disambiguationData":[TD([[subQ5,-1.0]])],"derivedFrom":subQ3}),1.0]])]});}
            var Q5;
            {var subQ1=sQuery(id+"F1.wireOp",EDGE,"E6");var subQ3=sQuery(id+"F1.wireOp",EDGE,"E33");var subQ4=makeQuery(id+"F1.imprint","INTERSECT",VERTEX,{"derivedFrom":[subQ1,subQ3]});Q5=makeQuery(id+"F1.imprint","IMPRINT",FACE,{"disambiguationData":[TD([[makeQuery(id+"F1.imprint","IMPRINT",EDGE,{"disambiguationData":[TD([[subQ4,-1.0]])],"derivedFrom":subQ3}),-1.0]])]});}
            var Q6;
            {var subQ0=sQuery(id+"F1.wireOp",EDGE,"E19");var subQ1=sQuery(id+"F1.wireOp",EDGE,"E0");var subQ2=makeQuery(id+"F1.imprint","INTERSECT",VERTEX,{"derivedFrom":[subQ1,subQ0]});Q6=makeQuery(id+"F1.imprint","IMPRINT",FACE,{"disambiguationData":[TD([[makeQuery(id+"F1.imprint","IMPRINT",EDGE,{"disambiguationData":[TD([[subQ2,1.0]])],"derivedFrom":subQ1}),1.0]])]});}
            var Q7;
            {var subQ0=sQuery(id+"F1.wireOp",EDGE,"E22");var subQ1=sQuery(id+"F1.wireOp",EDGE,"E0");var subQ2=makeQuery(id+"F1.imprint","INTERSECT",VERTEX,{"derivedFrom":[subQ1,subQ0]});Q7=makeQuery(id+"F1.imprint","IMPRINT",FACE,{"disambiguationData":[TD([[makeQuery(id+"F1.imprint","IMPRINT",EDGE,{"disambiguationData":[TD([[subQ2,-1.0]])],"derivedFrom":subQ1}),1.0]])]});}
            var Q8;
            {var subQ0=sQuery(id+"F1.wireOp",EDGE,"E21");var subQ1=sQuery(id+"F1.wireOp",EDGE,"E0");var subQ2=makeQuery(id+"F1.imprint","INTERSECT",VERTEX,{"derivedFrom":[subQ1,subQ0]});Q8=makeQuery(id+"F1.imprint","IMPRINT",FACE,{"disambiguationData":[TD([[makeQuery(id+"F1.imprint","IMPRINT",EDGE,{"disambiguationData":[TD([[subQ2,1.0]])],"derivedFrom":subQ1}),1.0]])]});}
            var Q9;
            {var subQ0=sQuery(id+"F1.wireOp",EDGE,"E20");var subQ1=sQuery(id+"F1.wireOp",EDGE,"E0");var subQ2=makeQuery(id+"F1.imprint","INTERSECT",VERTEX,{"derivedFrom":[subQ1,subQ0]});Q9=makeQuery(id+"F1.imprint","IMPRINT",FACE,{"disambiguationData":[TD([[makeQuery(id+"F1.imprint","IMPRINT",EDGE,{"disambiguationData":[TD([[subQ2,-1.0]])],"derivedFrom":subQ1}),1.0]])]});}
            extrude(context, id + "F29", {"entities" : qUnion([Q0, Q1, Q2, Q3, Q4, Q5, Q6, Q7, Q8, Q9]), "operationType" : NewBodyOperationType.REMOVE, "endBound" : BoundingType.THROUGH_ALL, "depth" : 25.4 * mm});
        }
        {
            var Q0;
            {var subQ0=sQuery(id+"F1.wireOp",EDGE,"E7");var subQ1=sQuery(id+"F1.wireOp",EDGE,"E0");var subQ2=makeQuery(id+"F1.imprint","INTERSECT",VERTEX,{"derivedFrom":[subQ1,subQ0]});Q0=makeQuery(id+"F1.imprint","IMPRINT",FACE,{"disambiguationData":[TD([[makeQuery(id+"F1.imprint","IMPRINT",EDGE,{"disambiguationData":[TD([[subQ2,1.0]])],"derivedFrom":subQ1}),1.0]])]});}
            var Q1;
            {var subQ0=sQuery(id+"F1.wireOp",EDGE,"E6");var subQ1=sQuery(id+"F1.wireOp",EDGE,"E0");var subQ2=makeQuery(id+"F1.imprint","INTERSECT",VERTEX,{"derivedFrom":[subQ1,subQ0]});Q1=makeQuery(id+"F1.imprint","IMPRINT",FACE,{"disambiguationData":[TD([[makeQuery(id+"F1.imprint","IMPRINT",EDGE,{"disambiguationData":[TD([[subQ2,-1.0]])],"derivedFrom":subQ1}),1.0]])]});}
            var Q2;
            {var subQ0=sQuery(id+"F1.wireOp",EDGE,"E4");var subQ1=sQuery(id+"F1.wireOp",EDGE,"E0");var subQ2=makeQuery(id+"F1.imprint","INTERSECT",VERTEX,{"derivedFrom":[subQ1,subQ0]});Q2=makeQuery(id+"F1.imprint","IMPRINT",FACE,{"disambiguationData":[TD([[makeQuery(id+"F1.imprint","IMPRINT",EDGE,{"disambiguationData":[TD([[subQ2,1.0]])],"derivedFrom":subQ1}),1.0]])]});}
            var Q3;
            {var subQ0=sQuery(id+"F1.wireOp",EDGE,"E5");var subQ1=sQuery(id+"F1.wireOp",EDGE,"E0");var subQ2=makeQuery(id+"F1.imprint","INTERSECT",VERTEX,{"derivedFrom":[subQ1,subQ0]});Q3=makeQuery(id+"F1.imprint","IMPRINT",FACE,{"disambiguationData":[TD([[makeQuery(id+"F1.imprint","IMPRINT",EDGE,{"disambiguationData":[TD([[subQ2,-1.0]])],"derivedFrom":subQ1}),1.0]])]});}
            extrude(context, id + "F30", {"entities" : qUnion([Q0, Q1, Q2, Q3]), "operationType" : NewBodyOperationType.REMOVE, "depth" : 25.4 * mm});
        }
    });
